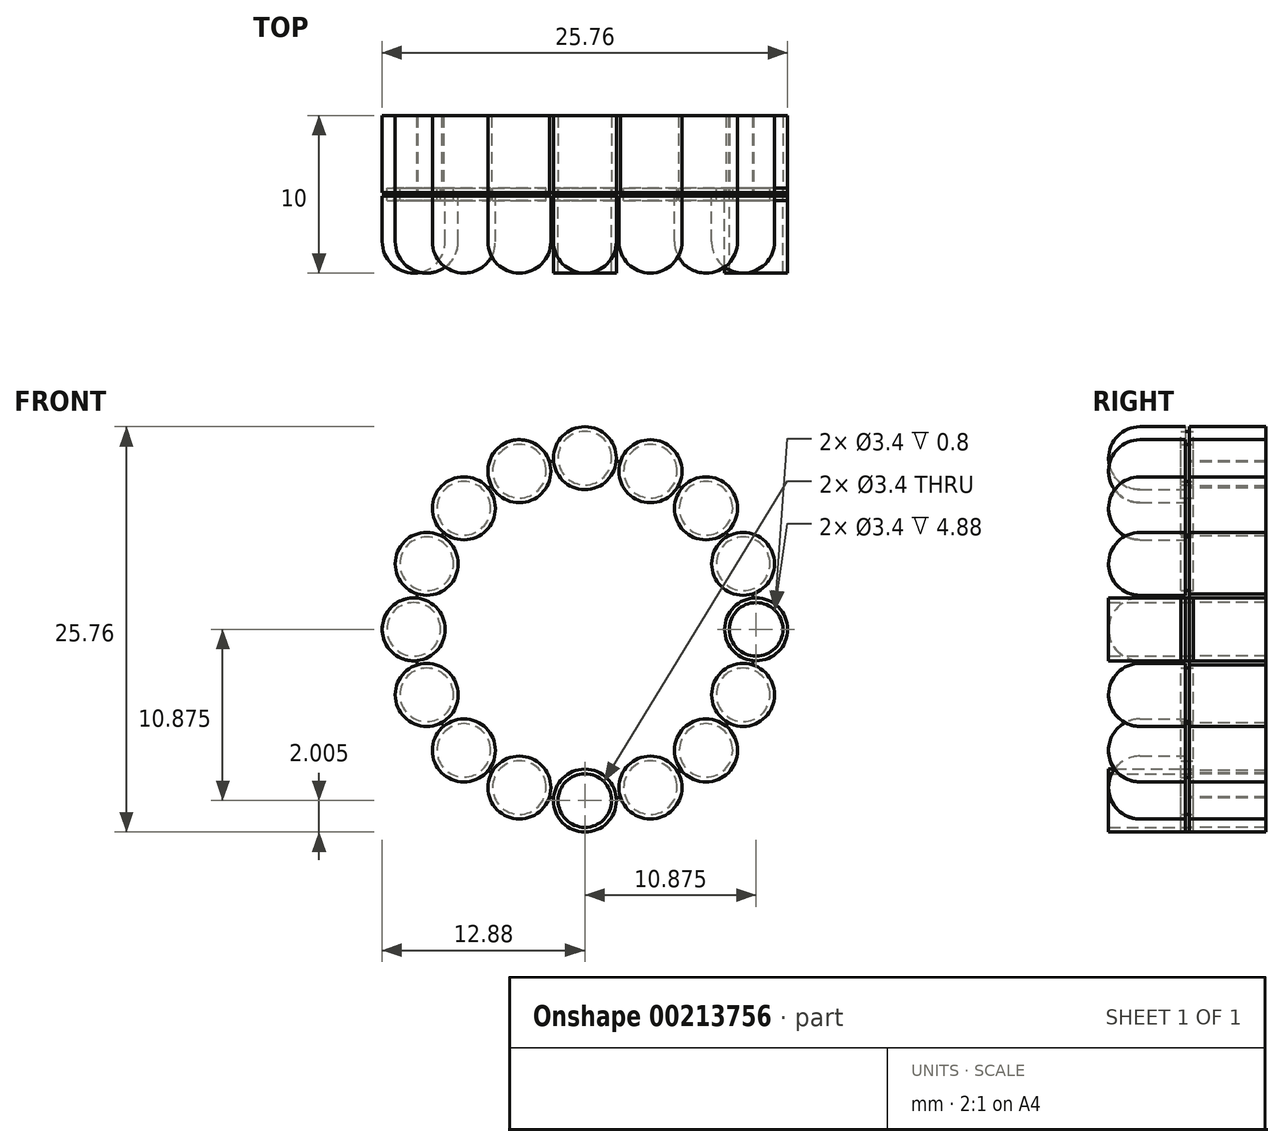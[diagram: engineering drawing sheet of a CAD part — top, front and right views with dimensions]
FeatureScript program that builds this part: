
annotation { "Feature Type Name" : "Feature", "Feature Type Description" : "" }
export const myFeature = defineFeature(function(context is Context, id is Id, definition is map)
    precondition{}
    {
        {
            var Q0;
            Q0=qCreatedBy(makeId("Front.planeOp"),FACE);
            var sketch = newSketch(context, id + "F0", { "sketchPlane" : qUnion([Q0])});
            skCircle(sketch, "E0", {"center": v(0, 0) * mm, "radius": 8.88 * mm, "construction": true});
            skCircle(sketch, "E1.0", {"center": v(0, 0) * mm, "radius": 12.88 * mm, "construction": true});
            skCircle(sketch, "E2.0", {"center": v(0, 0) * mm, "radius": 10.88 * mm});
            skCircle(sketch, "E3", {"center": v(0, 10.88) * mm, "radius": 2 * mm});
            skCircle(sketch, "E4.1.0", {"center": v(-4.16, 10.05) * mm, "radius": 2 * mm});
            skCircle(sketch, "E4.2.0", {"center": v(-7.69, 7.69) * mm, "radius": 2 * mm});
            skCircle(sketch, "E4.3.0", {"center": v(-10.05, 4.16) * mm, "radius": 2 * mm});
            skCircle(sketch, "E4.4.0", {"center": v(-10.88, 0) * mm, "radius": 2 * mm});
            skCircle(sketch, "E4.5.0", {"center": v(-10.05, -4.16) * mm, "radius": 2 * mm});
            skCircle(sketch, "E4.6.0", {"center": v(-7.69, -7.69) * mm, "radius": 2 * mm});
            skCircle(sketch, "E4.7.0", {"center": v(-4.16, -10.05) * mm, "radius": 2 * mm});
            skCircle(sketch, "E4.8.0", {"center": v(0, -10.88) * mm, "radius": 2 * mm});
            skCircle(sketch, "E4.9.0", {"center": v(4.16, -10.05) * mm, "radius": 2 * mm});
            skCircle(sketch, "E4.10.0", {"center": v(7.69, -7.69) * mm, "radius": 2 * mm});
            skCircle(sketch, "E4.11.0", {"center": v(10.05, -4.16) * mm, "radius": 2 * mm});
            skCircle(sketch, "E4.12.0", {"center": v(10.88, 0) * mm, "radius": 2 * mm});
            skCircle(sketch, "E4.13.0", {"center": v(10.05, 4.16) * mm, "radius": 2 * mm});
            skCircle(sketch, "E4.14.0", {"center": v(7.69, 7.69) * mm, "radius": 2 * mm});
            skCircle(sketch, "E4.15.0", {"center": v(4.16, 10.05) * mm, "radius": 2 * mm});
            skCircle(sketch, "E5.0", {"center": v(0, -10.88) * mm, "radius": 1.7 * mm});
            skCircle(sketch, "E6.1.0", {"center": v(4.16, -10.05) * mm, "radius": 1.7 * mm});
            skCircle(sketch, "E6.2.0", {"center": v(7.69, -7.69) * mm, "radius": 1.7 * mm});
            skCircle(sketch, "E6.3.0", {"center": v(10.05, -4.16) * mm, "radius": 1.7 * mm});
            skCircle(sketch, "E6.4.0", {"center": v(10.88, 0) * mm, "radius": 1.7 * mm});
            skCircle(sketch, "E6.5.0", {"center": v(10.05, 4.16) * mm, "radius": 1.7 * mm});
            skCircle(sketch, "E6.6.0", {"center": v(7.69, 7.69) * mm, "radius": 1.7 * mm});
            skCircle(sketch, "E6.7.0", {"center": v(4.16, 10.05) * mm, "radius": 1.7 * mm});
            skCircle(sketch, "E6.8.0", {"center": v(0, 10.88) * mm, "radius": 1.7 * mm});
            skCircle(sketch, "E6.9.0", {"center": v(-4.16, 10.05) * mm, "radius": 1.7 * mm});
            skCircle(sketch, "E6.10.0", {"center": v(-7.69, 7.69) * mm, "radius": 1.7 * mm});
            skCircle(sketch, "E6.11.0", {"center": v(-10.05, 4.16) * mm, "radius": 1.7 * mm});
            skCircle(sketch, "E6.12.0", {"center": v(-10.88, 0) * mm, "radius": 1.7 * mm});
            skCircle(sketch, "E6.13.0", {"center": v(-10.05, -4.16) * mm, "radius": 1.7 * mm});
            skCircle(sketch, "E6.14.0", {"center": v(-7.69, -7.69) * mm, "radius": 1.7 * mm});
            skCircle(sketch, "E6.15.0", {"center": v(-4.16, -10.05) * mm, "radius": 1.7 * mm});
            skSolve(sketch);
        }
        {
            var Q0;
            Q0=makeQuery(id+"F0.imprint","IMPRINT",FACE,{"disambiguationData":[TD([[makeQuery(id+"F0.imprint","IMPRINT",EDGE,{"derivedFrom":sQuery(id+"F0.wireOp",EDGE,"E3")}),1.0]])]});
            var Q1;
            Q1=makeQuery(id+"F0.imprint","IMPRINT",FACE,{"disambiguationData":[TD([[makeQuery(id+"F0.imprint","IMPRINT",EDGE,{"derivedFrom":sQuery(id+"F0.wireOp",EDGE,"E4.15.0")}),1.0]])]});
            var Q2;
            Q2=makeQuery(id+"F0.imprint","IMPRINT",FACE,{"disambiguationData":[TD([[makeQuery(id+"F0.imprint","IMPRINT",EDGE,{"derivedFrom":sQuery(id+"F0.wireOp",EDGE,"E4.14.0")}),1.0]])]});
            var Q3;
            Q3=makeQuery(id+"F0.imprint","IMPRINT",FACE,{"disambiguationData":[TD([[makeQuery(id+"F0.imprint","IMPRINT",EDGE,{"derivedFrom":sQuery(id+"F0.wireOp",EDGE,"E4.13.0")}),1.0]])]});
            var Q4;
            Q4=makeQuery(id+"F0.imprint","IMPRINT",FACE,{"disambiguationData":[TD([[makeQuery(id+"F0.imprint","IMPRINT",EDGE,{"derivedFrom":sQuery(id+"F0.wireOp",EDGE,"E4.12.0")}),1.0]])]});
            var Q5;
            Q5=makeQuery(id+"F0.imprint","IMPRINT",FACE,{"disambiguationData":[TD([[makeQuery(id+"F0.imprint","IMPRINT",EDGE,{"derivedFrom":sQuery(id+"F0.wireOp",EDGE,"E4.11.0")}),1.0]])]});
            var Q6;
            Q6=makeQuery(id+"F0.imprint","IMPRINT",FACE,{"disambiguationData":[TD([[makeQuery(id+"F0.imprint","IMPRINT",EDGE,{"derivedFrom":sQuery(id+"F0.wireOp",EDGE,"E4.10.0")}),1.0]])]});
            var Q7;
            Q7=makeQuery(id+"F0.imprint","IMPRINT",FACE,{"disambiguationData":[TD([[makeQuery(id+"F0.imprint","IMPRINT",EDGE,{"derivedFrom":sQuery(id+"F0.wireOp",EDGE,"E4.9.0")}),1.0]])]});
            var Q8;
            Q8=makeQuery(id+"F0.imprint","IMPRINT",FACE,{"disambiguationData":[TD([[makeQuery(id+"F0.imprint","IMPRINT",EDGE,{"derivedFrom":sQuery(id+"F0.wireOp",EDGE,"E4.8.0")}),1.0]])]});
            var Q9;
            Q9=makeQuery(id+"F0.imprint","IMPRINT",FACE,{"disambiguationData":[TD([[makeQuery(id+"F0.imprint","IMPRINT",EDGE,{"derivedFrom":sQuery(id+"F0.wireOp",EDGE,"E4.7.0")}),1.0]])]});
            var Q10;
            Q10=makeQuery(id+"F0.imprint","IMPRINT",FACE,{"disambiguationData":[TD([[makeQuery(id+"F0.imprint","IMPRINT",EDGE,{"derivedFrom":sQuery(id+"F0.wireOp",EDGE,"E4.6.0")}),1.0]])]});
            var Q11;
            Q11=makeQuery(id+"F0.imprint","IMPRINT",FACE,{"disambiguationData":[TD([[makeQuery(id+"F0.imprint","IMPRINT",EDGE,{"derivedFrom":sQuery(id+"F0.wireOp",EDGE,"E4.5.0")}),1.0]])]});
            var Q12;
            Q12=makeQuery(id+"F0.imprint","IMPRINT",FACE,{"disambiguationData":[TD([[makeQuery(id+"F0.imprint","IMPRINT",EDGE,{"derivedFrom":sQuery(id+"F0.wireOp",EDGE,"E4.4.0")}),1.0]])]});
            var Q13;
            Q13=makeQuery(id+"F0.imprint","IMPRINT",FACE,{"disambiguationData":[TD([[makeQuery(id+"F0.imprint","IMPRINT",EDGE,{"derivedFrom":sQuery(id+"F0.wireOp",EDGE,"E4.3.0")}),1.0]])]});
            var Q14;
            Q14=makeQuery(id+"F0.imprint","IMPRINT",FACE,{"disambiguationData":[TD([[makeQuery(id+"F0.imprint","IMPRINT",EDGE,{"derivedFrom":sQuery(id+"F0.wireOp",EDGE,"E4.2.0")}),1.0]])]});
            var Q15;
            Q15=makeQuery(id+"F0.imprint","IMPRINT",FACE,{"disambiguationData":[TD([[makeQuery(id+"F0.imprint","IMPRINT",EDGE,{"derivedFrom":sQuery(id+"F0.wireOp",EDGE,"E4.1.0")}),1.0]])]});
            var Q16;
            {var subQ0=sQuery(id+"F0.wireOp",EDGE,"E6.3.0");var subQ1=sQuery(id+"F0.wireOp",EDGE,"E2.0");var subQ2=makeQuery(id+"F0.imprint","INTERSECT",VERTEX,{"disambiguationData":[OD(0.0)],"derivedFrom":[subQ1,subQ0]});Q16=makeQuery(id+"F0.imprint","IMPRINT",FACE,{"disambiguationData":[TD([[makeQuery(id+"F0.imprint","IMPRINT",EDGE,{"disambiguationData":[TD([[subQ2,-1.0]])],"derivedFrom":subQ1}),-1.0]])]});}
            var Q17;
            {var subQ0=sQuery(id+"F0.wireOp",EDGE,"E6.3.0");var subQ1=sQuery(id+"F0.wireOp",EDGE,"E2.0");var subQ2=makeQuery(id+"F0.imprint","INTERSECT",VERTEX,{"disambiguationData":[OD(0.0)],"derivedFrom":[subQ1,subQ0]});Q17=makeQuery(id+"F0.imprint","IMPRINT",FACE,{"disambiguationData":[TD([[makeQuery(id+"F0.imprint","IMPRINT",EDGE,{"disambiguationData":[TD([[subQ2,-1.0]])],"derivedFrom":subQ1}),1.0]])]});}
            var Q18;
            {var subQ0=sQuery(id+"F0.wireOp",EDGE,"E6.2.0");var subQ1=sQuery(id+"F0.wireOp",EDGE,"E2.0");var subQ2=makeQuery(id+"F0.imprint","INTERSECT",VERTEX,{"disambiguationData":[OD(0.0)],"derivedFrom":[subQ1,subQ0]});Q18=makeQuery(id+"F0.imprint","IMPRINT",FACE,{"disambiguationData":[TD([[makeQuery(id+"F0.imprint","IMPRINT",EDGE,{"disambiguationData":[TD([[subQ2,-1.0]])],"derivedFrom":subQ1}),-1.0]])]});}
            var Q19;
            {var subQ0=sQuery(id+"F0.wireOp",EDGE,"E6.2.0");var subQ1=sQuery(id+"F0.wireOp",EDGE,"E2.0");var subQ2=makeQuery(id+"F0.imprint","INTERSECT",VERTEX,{"disambiguationData":[OD(0.0)],"derivedFrom":[subQ1,subQ0]});Q19=makeQuery(id+"F0.imprint","IMPRINT",FACE,{"disambiguationData":[TD([[makeQuery(id+"F0.imprint","IMPRINT",EDGE,{"disambiguationData":[TD([[subQ2,-1.0]])],"derivedFrom":subQ1}),1.0]])]});}
            var Q20;
            {var subQ0=sQuery(id+"F0.wireOp",EDGE,"E6.1.0");var subQ1=sQuery(id+"F0.wireOp",EDGE,"E2.0");var subQ2=makeQuery(id+"F0.imprint","INTERSECT",VERTEX,{"disambiguationData":[OD(0.0)],"derivedFrom":[subQ1,subQ0]});Q20=makeQuery(id+"F0.imprint","IMPRINT",FACE,{"disambiguationData":[TD([[makeQuery(id+"F0.imprint","IMPRINT",EDGE,{"disambiguationData":[TD([[subQ2,-1.0]])],"derivedFrom":subQ1}),-1.0]])]});}
            var Q21;
            {var subQ0=sQuery(id+"F0.wireOp",EDGE,"E6.1.0");var subQ1=sQuery(id+"F0.wireOp",EDGE,"E2.0");var subQ2=makeQuery(id+"F0.imprint","INTERSECT",VERTEX,{"disambiguationData":[OD(0.0)],"derivedFrom":[subQ1,subQ0]});Q21=makeQuery(id+"F0.imprint","IMPRINT",FACE,{"disambiguationData":[TD([[makeQuery(id+"F0.imprint","IMPRINT",EDGE,{"disambiguationData":[TD([[subQ2,-1.0]])],"derivedFrom":subQ1}),1.0]])]});}
            var Q22;
            {var subQ0=sQuery(id+"F0.wireOp",EDGE,"E5.0");var subQ1=sQuery(id+"F0.wireOp",EDGE,"E2.0");var subQ2=makeQuery(id+"F0.imprint","INTERSECT",VERTEX,{"disambiguationData":[OD(0.0)],"derivedFrom":[subQ1,subQ0]});Q22=makeQuery(id+"F0.imprint","IMPRINT",FACE,{"disambiguationData":[TD([[makeQuery(id+"F0.imprint","IMPRINT",EDGE,{"disambiguationData":[TD([[subQ2,-1.0]])],"derivedFrom":subQ1}),-1.0]])]});}
            var Q23;
            {var subQ0=sQuery(id+"F0.wireOp",EDGE,"E5.0");var subQ1=sQuery(id+"F0.wireOp",EDGE,"E2.0");var subQ2=makeQuery(id+"F0.imprint","INTERSECT",VERTEX,{"disambiguationData":[OD(0.0)],"derivedFrom":[subQ1,subQ0]});Q23=makeQuery(id+"F0.imprint","IMPRINT",FACE,{"disambiguationData":[TD([[makeQuery(id+"F0.imprint","IMPRINT",EDGE,{"disambiguationData":[TD([[subQ2,-1.0]])],"derivedFrom":subQ1}),1.0]])]});}
            var Q24;
            {var subQ0=sQuery(id+"F0.wireOp",EDGE,"E6.15.0");var subQ1=sQuery(id+"F0.wireOp",EDGE,"E2.0");var subQ2=makeQuery(id+"F0.imprint","INTERSECT",VERTEX,{"disambiguationData":[OD(0.0)],"derivedFrom":[subQ1,subQ0]});Q24=makeQuery(id+"F0.imprint","IMPRINT",FACE,{"disambiguationData":[TD([[makeQuery(id+"F0.imprint","IMPRINT",EDGE,{"disambiguationData":[TD([[subQ2,-1.0]])],"derivedFrom":subQ1}),-1.0]])]});}
            var Q25;
            {var subQ0=sQuery(id+"F0.wireOp",EDGE,"E6.15.0");var subQ1=sQuery(id+"F0.wireOp",EDGE,"E2.0");var subQ2=makeQuery(id+"F0.imprint","INTERSECT",VERTEX,{"disambiguationData":[OD(0.0)],"derivedFrom":[subQ1,subQ0]});Q25=makeQuery(id+"F0.imprint","IMPRINT",FACE,{"disambiguationData":[TD([[makeQuery(id+"F0.imprint","IMPRINT",EDGE,{"disambiguationData":[TD([[subQ2,-1.0]])],"derivedFrom":subQ1}),1.0]])]});}
            var Q26;
            {var subQ0=sQuery(id+"F0.wireOp",EDGE,"E6.14.0");var subQ1=sQuery(id+"F0.wireOp",EDGE,"E2.0");var subQ2=makeQuery(id+"F0.imprint","INTERSECT",VERTEX,{"disambiguationData":[OD(0.0)],"derivedFrom":[subQ1,subQ0]});Q26=makeQuery(id+"F0.imprint","IMPRINT",FACE,{"disambiguationData":[TD([[makeQuery(id+"F0.imprint","IMPRINT",EDGE,{"disambiguationData":[TD([[subQ2,-1.0]])],"derivedFrom":subQ1}),-1.0]])]});}
            var Q27;
            {var subQ0=sQuery(id+"F0.wireOp",EDGE,"E6.14.0");var subQ1=sQuery(id+"F0.wireOp",EDGE,"E2.0");var subQ2=makeQuery(id+"F0.imprint","INTERSECT",VERTEX,{"disambiguationData":[OD(0.0)],"derivedFrom":[subQ1,subQ0]});Q27=makeQuery(id+"F0.imprint","IMPRINT",FACE,{"disambiguationData":[TD([[makeQuery(id+"F0.imprint","IMPRINT",EDGE,{"disambiguationData":[TD([[subQ2,-1.0]])],"derivedFrom":subQ1}),1.0]])]});}
            var Q28;
            {var subQ0=sQuery(id+"F0.wireOp",EDGE,"E6.13.0");var subQ1=sQuery(id+"F0.wireOp",EDGE,"E2.0");var subQ2=makeQuery(id+"F0.imprint","INTERSECT",VERTEX,{"disambiguationData":[OD(0.0)],"derivedFrom":[subQ1,subQ0]});Q28=makeQuery(id+"F0.imprint","IMPRINT",FACE,{"disambiguationData":[TD([[makeQuery(id+"F0.imprint","IMPRINT",EDGE,{"disambiguationData":[TD([[subQ2,-1.0]])],"derivedFrom":subQ1}),-1.0]])]});}
            var Q29;
            {var subQ0=sQuery(id+"F0.wireOp",EDGE,"E6.13.0");var subQ1=sQuery(id+"F0.wireOp",EDGE,"E2.0");var subQ2=makeQuery(id+"F0.imprint","INTERSECT",VERTEX,{"disambiguationData":[OD(0.0)],"derivedFrom":[subQ1,subQ0]});Q29=makeQuery(id+"F0.imprint","IMPRINT",FACE,{"disambiguationData":[TD([[makeQuery(id+"F0.imprint","IMPRINT",EDGE,{"disambiguationData":[TD([[subQ2,-1.0]])],"derivedFrom":subQ1}),1.0]])]});}
            var Q30;
            {var subQ0=sQuery(id+"F0.wireOp",EDGE,"E6.12.0");var subQ1=sQuery(id+"F0.wireOp",EDGE,"E2.0");var subQ2=makeQuery(id+"F0.imprint","INTERSECT",VERTEX,{"disambiguationData":[OD(0.0)],"derivedFrom":[subQ1,subQ0]});Q30=makeQuery(id+"F0.imprint","IMPRINT",FACE,{"disambiguationData":[TD([[makeQuery(id+"F0.imprint","IMPRINT",EDGE,{"disambiguationData":[TD([[subQ2,-1.0]])],"derivedFrom":subQ1}),-1.0]])]});}
            var Q31;
            {var subQ0=sQuery(id+"F0.wireOp",EDGE,"E6.12.0");var subQ1=sQuery(id+"F0.wireOp",EDGE,"E2.0");var subQ2=makeQuery(id+"F0.imprint","INTERSECT",VERTEX,{"disambiguationData":[OD(0.0)],"derivedFrom":[subQ1,subQ0]});Q31=makeQuery(id+"F0.imprint","IMPRINT",FACE,{"disambiguationData":[TD([[makeQuery(id+"F0.imprint","IMPRINT",EDGE,{"disambiguationData":[TD([[subQ2,-1.0]])],"derivedFrom":subQ1}),1.0]])]});}
            var Q32;
            {var subQ0=sQuery(id+"F0.wireOp",EDGE,"E6.11.0");var subQ1=sQuery(id+"F0.wireOp",EDGE,"E2.0");var subQ2=makeQuery(id+"F0.imprint","INTERSECT",VERTEX,{"disambiguationData":[OD(0.0)],"derivedFrom":[subQ1,subQ0]});Q32=makeQuery(id+"F0.imprint","IMPRINT",FACE,{"disambiguationData":[TD([[makeQuery(id+"F0.imprint","IMPRINT",EDGE,{"disambiguationData":[TD([[subQ2,-1.0]])],"derivedFrom":subQ1}),-1.0]])]});}
            var Q33;
            {var subQ0=sQuery(id+"F0.wireOp",EDGE,"E6.11.0");var subQ1=sQuery(id+"F0.wireOp",EDGE,"E2.0");var subQ2=makeQuery(id+"F0.imprint","INTERSECT",VERTEX,{"disambiguationData":[OD(0.0)],"derivedFrom":[subQ1,subQ0]});Q33=makeQuery(id+"F0.imprint","IMPRINT",FACE,{"disambiguationData":[TD([[makeQuery(id+"F0.imprint","IMPRINT",EDGE,{"disambiguationData":[TD([[subQ2,-1.0]])],"derivedFrom":subQ1}),1.0]])]});}
            var Q34;
            {var subQ0=sQuery(id+"F0.wireOp",EDGE,"E6.10.0");var subQ1=sQuery(id+"F0.wireOp",EDGE,"E2.0");var subQ2=makeQuery(id+"F0.imprint","INTERSECT",VERTEX,{"disambiguationData":[OD(0.0)],"derivedFrom":[subQ1,subQ0]});Q34=makeQuery(id+"F0.imprint","IMPRINT",FACE,{"disambiguationData":[TD([[makeQuery(id+"F0.imprint","IMPRINT",EDGE,{"disambiguationData":[TD([[subQ2,-1.0]])],"derivedFrom":subQ1}),-1.0]])]});}
            var Q35;
            {var subQ0=sQuery(id+"F0.wireOp",EDGE,"E6.10.0");var subQ1=sQuery(id+"F0.wireOp",EDGE,"E2.0");var subQ2=makeQuery(id+"F0.imprint","INTERSECT",VERTEX,{"disambiguationData":[OD(0.0)],"derivedFrom":[subQ1,subQ0]});Q35=makeQuery(id+"F0.imprint","IMPRINT",FACE,{"disambiguationData":[TD([[makeQuery(id+"F0.imprint","IMPRINT",EDGE,{"disambiguationData":[TD([[subQ2,-1.0]])],"derivedFrom":subQ1}),1.0]])]});}
            var Q36;
            {var subQ0=sQuery(id+"F0.wireOp",EDGE,"E6.9.0");var subQ1=sQuery(id+"F0.wireOp",EDGE,"E2.0");var subQ2=makeQuery(id+"F0.imprint","INTERSECT",VERTEX,{"disambiguationData":[OD(0.0)],"derivedFrom":[subQ1,subQ0]});Q36=makeQuery(id+"F0.imprint","IMPRINT",FACE,{"disambiguationData":[TD([[makeQuery(id+"F0.imprint","IMPRINT",EDGE,{"disambiguationData":[TD([[subQ2,-1.0]])],"derivedFrom":subQ1}),-1.0]])]});}
            var Q37;
            {var subQ0=sQuery(id+"F0.wireOp",EDGE,"E6.9.0");var subQ1=sQuery(id+"F0.wireOp",EDGE,"E2.0");var subQ2=makeQuery(id+"F0.imprint","INTERSECT",VERTEX,{"disambiguationData":[OD(0.0)],"derivedFrom":[subQ1,subQ0]});Q37=makeQuery(id+"F0.imprint","IMPRINT",FACE,{"disambiguationData":[TD([[makeQuery(id+"F0.imprint","IMPRINT",EDGE,{"disambiguationData":[TD([[subQ2,-1.0]])],"derivedFrom":subQ1}),1.0]])]});}
            var Q38;
            {var subQ0=sQuery(id+"F0.wireOp",EDGE,"E6.8.0");var subQ1=sQuery(id+"F0.wireOp",EDGE,"E2.0");var subQ2=makeQuery(id+"F0.imprint","INTERSECT",VERTEX,{"disambiguationData":[OD(0.0)],"derivedFrom":[subQ1,subQ0]});Q38=makeQuery(id+"F0.imprint","IMPRINT",FACE,{"disambiguationData":[TD([[makeQuery(id+"F0.imprint","IMPRINT",EDGE,{"disambiguationData":[TD([[subQ2,-1.0]])],"derivedFrom":subQ1}),-1.0]])]});}
            var Q39;
            {var subQ0=sQuery(id+"F0.wireOp",EDGE,"E6.8.0");var subQ1=sQuery(id+"F0.wireOp",EDGE,"E2.0");var subQ2=makeQuery(id+"F0.imprint","INTERSECT",VERTEX,{"disambiguationData":[OD(0.0)],"derivedFrom":[subQ1,subQ0]});Q39=makeQuery(id+"F0.imprint","IMPRINT",FACE,{"disambiguationData":[TD([[makeQuery(id+"F0.imprint","IMPRINT",EDGE,{"disambiguationData":[TD([[subQ2,-1.0]])],"derivedFrom":subQ1}),1.0]])]});}
            var Q40;
            {var subQ0=sQuery(id+"F0.wireOp",EDGE,"E6.7.0");var subQ1=sQuery(id+"F0.wireOp",EDGE,"E2.0");var subQ2=makeQuery(id+"F0.imprint","INTERSECT",VERTEX,{"disambiguationData":[OD(0.0)],"derivedFrom":[subQ1,subQ0]});Q40=makeQuery(id+"F0.imprint","IMPRINT",FACE,{"disambiguationData":[TD([[makeQuery(id+"F0.imprint","IMPRINT",EDGE,{"disambiguationData":[TD([[subQ2,-1.0]])],"derivedFrom":subQ1}),-1.0]])]});}
            var Q41;
            {var subQ0=sQuery(id+"F0.wireOp",EDGE,"E6.7.0");var subQ1=sQuery(id+"F0.wireOp",EDGE,"E2.0");var subQ2=makeQuery(id+"F0.imprint","INTERSECT",VERTEX,{"disambiguationData":[OD(0.0)],"derivedFrom":[subQ1,subQ0]});Q41=makeQuery(id+"F0.imprint","IMPRINT",FACE,{"disambiguationData":[TD([[makeQuery(id+"F0.imprint","IMPRINT",EDGE,{"disambiguationData":[TD([[subQ2,-1.0]])],"derivedFrom":subQ1}),1.0]])]});}
            var Q42;
            {var subQ0=sQuery(id+"F0.wireOp",EDGE,"E6.6.0");var subQ1=sQuery(id+"F0.wireOp",EDGE,"E2.0");var subQ2=makeQuery(id+"F0.imprint","INTERSECT",VERTEX,{"disambiguationData":[OD(0.0)],"derivedFrom":[subQ1,subQ0]});Q42=makeQuery(id+"F0.imprint","IMPRINT",FACE,{"disambiguationData":[TD([[makeQuery(id+"F0.imprint","IMPRINT",EDGE,{"disambiguationData":[TD([[subQ2,-1.0]])],"derivedFrom":subQ1}),-1.0]])]});}
            var Q43;
            {var subQ0=sQuery(id+"F0.wireOp",EDGE,"E6.6.0");var subQ1=sQuery(id+"F0.wireOp",EDGE,"E2.0");var subQ2=makeQuery(id+"F0.imprint","INTERSECT",VERTEX,{"disambiguationData":[OD(0.0)],"derivedFrom":[subQ1,subQ0]});Q43=makeQuery(id+"F0.imprint","IMPRINT",FACE,{"disambiguationData":[TD([[makeQuery(id+"F0.imprint","IMPRINT",EDGE,{"disambiguationData":[TD([[subQ2,-1.0]])],"derivedFrom":subQ1}),1.0]])]});}
            var Q44;
            {var subQ0=sQuery(id+"F0.wireOp",EDGE,"E6.5.0");var subQ1=sQuery(id+"F0.wireOp",EDGE,"E2.0");var subQ2=makeQuery(id+"F0.imprint","INTERSECT",VERTEX,{"disambiguationData":[OD(0.0)],"derivedFrom":[subQ1,subQ0]});Q44=makeQuery(id+"F0.imprint","IMPRINT",FACE,{"disambiguationData":[TD([[makeQuery(id+"F0.imprint","IMPRINT",EDGE,{"disambiguationData":[TD([[subQ2,-1.0]])],"derivedFrom":subQ1}),-1.0]])]});}
            var Q45;
            {var subQ0=sQuery(id+"F0.wireOp",EDGE,"E6.5.0");var subQ1=sQuery(id+"F0.wireOp",EDGE,"E2.0");var subQ2=makeQuery(id+"F0.imprint","INTERSECT",VERTEX,{"disambiguationData":[OD(0.0)],"derivedFrom":[subQ1,subQ0]});Q45=makeQuery(id+"F0.imprint","IMPRINT",FACE,{"disambiguationData":[TD([[makeQuery(id+"F0.imprint","IMPRINT",EDGE,{"disambiguationData":[TD([[subQ2,-1.0]])],"derivedFrom":subQ1}),1.0]])]});}
            var Q46;
            {var subQ0=sQuery(id+"F0.wireOp",EDGE,"E6.4.0");var subQ1=sQuery(id+"F0.wireOp",EDGE,"E2.0");var subQ2=makeQuery(id+"F0.imprint","INTERSECT",VERTEX,{"disambiguationData":[OD(0.0)],"derivedFrom":[subQ1,subQ0]});Q46=makeQuery(id+"F0.imprint","IMPRINT",FACE,{"disambiguationData":[TD([[makeQuery(id+"F0.imprint","IMPRINT",EDGE,{"disambiguationData":[TD([[subQ2,1.0]])],"derivedFrom":subQ1}),-1.0]])]});}
            var Q47;
            {var subQ0=sQuery(id+"F0.wireOp",EDGE,"E6.4.0");var subQ1=sQuery(id+"F0.wireOp",EDGE,"E2.0");var subQ2=makeQuery(id+"F0.imprint","INTERSECT",VERTEX,{"disambiguationData":[OD(0.0)],"derivedFrom":[subQ1,subQ0]});Q47=makeQuery(id+"F0.imprint","IMPRINT",FACE,{"disambiguationData":[TD([[makeQuery(id+"F0.imprint","IMPRINT",EDGE,{"disambiguationData":[TD([[subQ2,1.0]])],"derivedFrom":subQ1}),1.0]])]});}
            extrude(context, id + "F1", {"entities" : qUnion([Q0, Q1, Q2, Q3, Q4, Q5, Q6, Q7, Q8, Q9, Q10, Q11, Q12, Q13, Q14, Q15, Q16, Q17, Q18, Q19, Q20, Q21, Q22, Q23, Q24, Q25, Q26, Q27, Q28, Q29, Q30, Q31, Q32, Q33, Q34, Q35, Q36, Q37, Q38, Q39, Q40, Q41, Q42, Q43, Q44, Q45, Q46, Q47]), "depth" : 5 * mm, "hasSecondDirection" : true, "secondDirectionOppositeDirection" : false, "secondDirectionDepth" : .12 * mm});
        }
        {
            var Q0;
            Q0=qCreatedBy(makeId("Right.planeOp"),FACE);
            var sketch = newSketch(context, id + "F2", { "sketchPlane" : qUnion([Q0])});
            skPoint(sketch, "E7", {"position": v(0, -10.88) * mm});
            skLineSegment(sketch, "E8.bottom", {"start": v(-2.5, -11.28) * mm, "end": v(2.5, -11.28) * mm});
            skLineSegment(sketch, "E8.top", {"start": v(-2.5, -10.47) * mm, "end": v(2.5, -10.47) * mm});
            skLineSegment(sketch, "E8.left", {"start": v(-2.5, -11.28) * mm, "end": v(-2.5, -10.47) * mm});
            skLineSegment(sketch, "E8.right", {"start": v(2.5, -11.28) * mm, "end": v(2.5, -10.47) * mm});
            skSolve(sketch);
        }
        {
            var Q0;
            Q0=sQuery(id+"F2.wireOp",EDGE,"E8.right");
            var Q1;
            Q1=sQuery(id+"F2.wireOp",EDGE,"E8.bottom");
            var Q2;
            Q2=sQuery(id+"F2.wireOp",EDGE,"E8.top");
            var Q3;
            Q3=sQuery(id+"F2.wireOp",EDGE,"E8.left");
            var Q4;
            Q4=sQuery(id+"F0.wireOp",EDGE,"E2.0");
            revolve(context, id + "F3", {"bodyType" : ToolBodyType.SURFACE, "surfaceEntities" : qUnion([Q0, Q1, Q2, Q3]), "axis" : qUnion([Q4]), "revolveType" : RevolveType.FULL});
        }
        {
            var Q0;
            {var subQ0=sQuery(id+"F0.wireOp",EDGE,"E6.3.0");var subQ1=sQuery(id+"F0.wireOp",EDGE,"E2.0");var subQ2=makeQuery(id+"F0.imprint","INTERSECT",VERTEX,{"disambiguationData":[OD(0.0)],"derivedFrom":[subQ1,subQ0]});Q0=makeQuery(id+"F0.imprint","IMPRINT",FACE,{"disambiguationData":[TD([[makeQuery(id+"F0.imprint","IMPRINT",EDGE,{"disambiguationData":[TD([[subQ2,-1.0]])],"derivedFrom":subQ1}),-1.0]])]});}
            var Q1;
            {var subQ0=sQuery(id+"F0.wireOp",EDGE,"E4.11.0");var subQ1=sQuery(id+"F0.wireOp",EDGE,"E2.0");var subQ2=makeQuery(id+"F0.imprint","INTERSECT",VERTEX,{"disambiguationData":[OD(0.0)],"derivedFrom":[subQ1,subQ0]});Q1=makeQuery(id+"F0.imprint","IMPRINT",FACE,{"disambiguationData":[TD([[makeQuery(id+"F0.imprint","IMPRINT",EDGE,{"disambiguationData":[TD([[subQ2,-1.0]])],"derivedFrom":subQ1}),-1.0]])]});}
            var Q2;
            {var subQ0=sQuery(id+"F0.wireOp",EDGE,"E6.3.0");var subQ1=sQuery(id+"F0.wireOp",EDGE,"E2.0");var subQ2=makeQuery(id+"F0.imprint","INTERSECT",VERTEX,{"disambiguationData":[OD(0.0)],"derivedFrom":[subQ1,subQ0]});Q2=makeQuery(id+"F0.imprint","IMPRINT",FACE,{"disambiguationData":[TD([[makeQuery(id+"F0.imprint","IMPRINT",EDGE,{"disambiguationData":[TD([[subQ2,-1.0]])],"derivedFrom":subQ1}),1.0]])]});}
            var Q3;
            {var subQ0=sQuery(id+"F0.wireOp",EDGE,"E4.11.0");var subQ1=sQuery(id+"F0.wireOp",EDGE,"E2.0");var subQ2=makeQuery(id+"F0.imprint","INTERSECT",VERTEX,{"disambiguationData":[OD(0.0)],"derivedFrom":[subQ1,subQ0]});Q3=makeQuery(id+"F0.imprint","IMPRINT",FACE,{"disambiguationData":[TD([[makeQuery(id+"F0.imprint","IMPRINT",EDGE,{"disambiguationData":[TD([[subQ2,-1.0]])],"derivedFrom":subQ1}),1.0]])]});}
            var Q4;
            {var subQ0=sQuery(id+"F0.wireOp",EDGE,"E4.10.0");var subQ1=sQuery(id+"F0.wireOp",EDGE,"E2.0");var subQ2=makeQuery(id+"F0.imprint","INTERSECT",VERTEX,{"disambiguationData":[OD(0.0)],"derivedFrom":[subQ1,subQ0]});Q4=makeQuery(id+"F0.imprint","IMPRINT",FACE,{"disambiguationData":[TD([[makeQuery(id+"F0.imprint","IMPRINT",EDGE,{"disambiguationData":[TD([[subQ2,-1.0]])],"derivedFrom":subQ1}),1.0]])]});}
            var Q5;
            {var subQ0=sQuery(id+"F0.wireOp",EDGE,"E6.2.0");var subQ1=sQuery(id+"F0.wireOp",EDGE,"E2.0");var subQ2=makeQuery(id+"F0.imprint","INTERSECT",VERTEX,{"disambiguationData":[OD(0.0)],"derivedFrom":[subQ1,subQ0]});Q5=makeQuery(id+"F0.imprint","IMPRINT",FACE,{"disambiguationData":[TD([[makeQuery(id+"F0.imprint","IMPRINT",EDGE,{"disambiguationData":[TD([[subQ2,-1.0]])],"derivedFrom":subQ1}),1.0]])]});}
            var Q6;
            {var subQ0=sQuery(id+"F0.wireOp",EDGE,"E6.2.0");var subQ1=sQuery(id+"F0.wireOp",EDGE,"E2.0");var subQ2=makeQuery(id+"F0.imprint","INTERSECT",VERTEX,{"disambiguationData":[OD(0.0)],"derivedFrom":[subQ1,subQ0]});Q6=makeQuery(id+"F0.imprint","IMPRINT",FACE,{"disambiguationData":[TD([[makeQuery(id+"F0.imprint","IMPRINT",EDGE,{"disambiguationData":[TD([[subQ2,-1.0]])],"derivedFrom":subQ1}),-1.0]])]});}
            var Q7;
            {var subQ0=sQuery(id+"F0.wireOp",EDGE,"E4.10.0");var subQ1=sQuery(id+"F0.wireOp",EDGE,"E2.0");var subQ2=makeQuery(id+"F0.imprint","INTERSECT",VERTEX,{"disambiguationData":[OD(0.0)],"derivedFrom":[subQ1,subQ0]});Q7=makeQuery(id+"F0.imprint","IMPRINT",FACE,{"disambiguationData":[TD([[makeQuery(id+"F0.imprint","IMPRINT",EDGE,{"disambiguationData":[TD([[subQ2,-1.0]])],"derivedFrom":subQ1}),-1.0]])]});}
            var Q8;
            {var subQ0=sQuery(id+"F0.wireOp",EDGE,"E4.9.0");var subQ1=sQuery(id+"F0.wireOp",EDGE,"E2.0");var subQ2=makeQuery(id+"F0.imprint","INTERSECT",VERTEX,{"disambiguationData":[OD(0.0)],"derivedFrom":[subQ1,subQ0]});Q8=makeQuery(id+"F0.imprint","IMPRINT",FACE,{"disambiguationData":[TD([[makeQuery(id+"F0.imprint","IMPRINT",EDGE,{"disambiguationData":[TD([[subQ2,-1.0]])],"derivedFrom":subQ1}),-1.0]])]});}
            var Q9;
            {var subQ0=sQuery(id+"F0.wireOp",EDGE,"E6.1.0");var subQ1=sQuery(id+"F0.wireOp",EDGE,"E2.0");var subQ2=makeQuery(id+"F0.imprint","INTERSECT",VERTEX,{"disambiguationData":[OD(0.0)],"derivedFrom":[subQ1,subQ0]});Q9=makeQuery(id+"F0.imprint","IMPRINT",FACE,{"disambiguationData":[TD([[makeQuery(id+"F0.imprint","IMPRINT",EDGE,{"disambiguationData":[TD([[subQ2,-1.0]])],"derivedFrom":subQ1}),-1.0]])]});}
            var Q10;
            {var subQ0=sQuery(id+"F0.wireOp",EDGE,"E6.1.0");var subQ1=sQuery(id+"F0.wireOp",EDGE,"E2.0");var subQ2=makeQuery(id+"F0.imprint","INTERSECT",VERTEX,{"disambiguationData":[OD(0.0)],"derivedFrom":[subQ1,subQ0]});Q10=makeQuery(id+"F0.imprint","IMPRINT",FACE,{"disambiguationData":[TD([[makeQuery(id+"F0.imprint","IMPRINT",EDGE,{"disambiguationData":[TD([[subQ2,-1.0]])],"derivedFrom":subQ1}),1.0]])]});}
            var Q11;
            {var subQ0=sQuery(id+"F0.wireOp",EDGE,"E4.9.0");var subQ1=sQuery(id+"F0.wireOp",EDGE,"E2.0");var subQ2=makeQuery(id+"F0.imprint","INTERSECT",VERTEX,{"disambiguationData":[OD(0.0)],"derivedFrom":[subQ1,subQ0]});Q11=makeQuery(id+"F0.imprint","IMPRINT",FACE,{"disambiguationData":[TD([[makeQuery(id+"F0.imprint","IMPRINT",EDGE,{"disambiguationData":[TD([[subQ2,-1.0]])],"derivedFrom":subQ1}),1.0]])]});}
            var Q12;
            {var subQ0=sQuery(id+"F0.wireOp",EDGE,"E5.0");var subQ1=sQuery(id+"F0.wireOp",EDGE,"E2.0");var subQ2=makeQuery(id+"F0.imprint","INTERSECT",VERTEX,{"disambiguationData":[OD(0.0)],"derivedFrom":[subQ1,subQ0]});Q12=makeQuery(id+"F0.imprint","IMPRINT",FACE,{"disambiguationData":[TD([[makeQuery(id+"F0.imprint","IMPRINT",EDGE,{"disambiguationData":[TD([[subQ2,-1.0]])],"derivedFrom":subQ1}),1.0]])]});}
            var Q13;
            {var subQ0=sQuery(id+"F0.wireOp",EDGE,"E5.0");var subQ1=sQuery(id+"F0.wireOp",EDGE,"E2.0");var subQ2=makeQuery(id+"F0.imprint","INTERSECT",VERTEX,{"disambiguationData":[OD(0.0)],"derivedFrom":[subQ1,subQ0]});Q13=makeQuery(id+"F0.imprint","IMPRINT",FACE,{"disambiguationData":[TD([[makeQuery(id+"F0.imprint","IMPRINT",EDGE,{"disambiguationData":[TD([[subQ2,-1.0]])],"derivedFrom":subQ1}),-1.0]])]});}
            var Q14;
            {var subQ0=sQuery(id+"F0.wireOp",EDGE,"E4.8.0");var subQ1=sQuery(id+"F0.wireOp",EDGE,"E2.0");var subQ2=makeQuery(id+"F0.imprint","INTERSECT",VERTEX,{"disambiguationData":[OD(0.0)],"derivedFrom":[subQ1,subQ0]});Q14=makeQuery(id+"F0.imprint","IMPRINT",FACE,{"disambiguationData":[TD([[makeQuery(id+"F0.imprint","IMPRINT",EDGE,{"disambiguationData":[TD([[subQ2,-1.0]])],"derivedFrom":subQ1}),-1.0]])]});}
            var Q15;
            {var subQ0=sQuery(id+"F0.wireOp",EDGE,"E4.8.0");var subQ1=sQuery(id+"F0.wireOp",EDGE,"E2.0");var subQ2=makeQuery(id+"F0.imprint","INTERSECT",VERTEX,{"disambiguationData":[OD(0.0)],"derivedFrom":[subQ1,subQ0]});Q15=makeQuery(id+"F0.imprint","IMPRINT",FACE,{"disambiguationData":[TD([[makeQuery(id+"F0.imprint","IMPRINT",EDGE,{"disambiguationData":[TD([[subQ2,-1.0]])],"derivedFrom":subQ1}),1.0]])]});}
            var Q16;
            {var subQ0=sQuery(id+"F0.wireOp",EDGE,"E4.7.0");var subQ1=sQuery(id+"F0.wireOp",EDGE,"E2.0");var subQ2=makeQuery(id+"F0.imprint","INTERSECT",VERTEX,{"disambiguationData":[OD(0.0)],"derivedFrom":[subQ1,subQ0]});Q16=makeQuery(id+"F0.imprint","IMPRINT",FACE,{"disambiguationData":[TD([[makeQuery(id+"F0.imprint","IMPRINT",EDGE,{"disambiguationData":[TD([[subQ2,-1.0]])],"derivedFrom":subQ1}),1.0]])]});}
            var Q17;
            {var subQ0=sQuery(id+"F0.wireOp",EDGE,"E6.15.0");var subQ1=sQuery(id+"F0.wireOp",EDGE,"E2.0");var subQ2=makeQuery(id+"F0.imprint","INTERSECT",VERTEX,{"disambiguationData":[OD(0.0)],"derivedFrom":[subQ1,subQ0]});Q17=makeQuery(id+"F0.imprint","IMPRINT",FACE,{"disambiguationData":[TD([[makeQuery(id+"F0.imprint","IMPRINT",EDGE,{"disambiguationData":[TD([[subQ2,-1.0]])],"derivedFrom":subQ1}),1.0]])]});}
            var Q18;
            {var subQ0=sQuery(id+"F0.wireOp",EDGE,"E6.15.0");var subQ1=sQuery(id+"F0.wireOp",EDGE,"E2.0");var subQ2=makeQuery(id+"F0.imprint","INTERSECT",VERTEX,{"disambiguationData":[OD(0.0)],"derivedFrom":[subQ1,subQ0]});Q18=makeQuery(id+"F0.imprint","IMPRINT",FACE,{"disambiguationData":[TD([[makeQuery(id+"F0.imprint","IMPRINT",EDGE,{"disambiguationData":[TD([[subQ2,-1.0]])],"derivedFrom":subQ1}),-1.0]])]});}
            var Q19;
            {var subQ0=sQuery(id+"F0.wireOp",EDGE,"E4.7.0");var subQ1=sQuery(id+"F0.wireOp",EDGE,"E2.0");var subQ2=makeQuery(id+"F0.imprint","INTERSECT",VERTEX,{"disambiguationData":[OD(0.0)],"derivedFrom":[subQ1,subQ0]});Q19=makeQuery(id+"F0.imprint","IMPRINT",FACE,{"disambiguationData":[TD([[makeQuery(id+"F0.imprint","IMPRINT",EDGE,{"disambiguationData":[TD([[subQ2,-1.0]])],"derivedFrom":subQ1}),-1.0]])]});}
            var Q20;
            {var subQ0=sQuery(id+"F0.wireOp",EDGE,"E4.6.0");var subQ1=sQuery(id+"F0.wireOp",EDGE,"E2.0");var subQ2=makeQuery(id+"F0.imprint","INTERSECT",VERTEX,{"disambiguationData":[OD(0.0)],"derivedFrom":[subQ1,subQ0]});Q20=makeQuery(id+"F0.imprint","IMPRINT",FACE,{"disambiguationData":[TD([[makeQuery(id+"F0.imprint","IMPRINT",EDGE,{"disambiguationData":[TD([[subQ2,-1.0]])],"derivedFrom":subQ1}),-1.0]])]});}
            var Q21;
            {var subQ0=sQuery(id+"F0.wireOp",EDGE,"E6.14.0");var subQ1=sQuery(id+"F0.wireOp",EDGE,"E2.0");var subQ2=makeQuery(id+"F0.imprint","INTERSECT",VERTEX,{"disambiguationData":[OD(0.0)],"derivedFrom":[subQ1,subQ0]});Q21=makeQuery(id+"F0.imprint","IMPRINT",FACE,{"disambiguationData":[TD([[makeQuery(id+"F0.imprint","IMPRINT",EDGE,{"disambiguationData":[TD([[subQ2,-1.0]])],"derivedFrom":subQ1}),-1.0]])]});}
            var Q22;
            {var subQ0=sQuery(id+"F0.wireOp",EDGE,"E6.14.0");var subQ1=sQuery(id+"F0.wireOp",EDGE,"E2.0");var subQ2=makeQuery(id+"F0.imprint","INTERSECT",VERTEX,{"disambiguationData":[OD(0.0)],"derivedFrom":[subQ1,subQ0]});Q22=makeQuery(id+"F0.imprint","IMPRINT",FACE,{"disambiguationData":[TD([[makeQuery(id+"F0.imprint","IMPRINT",EDGE,{"disambiguationData":[TD([[subQ2,-1.0]])],"derivedFrom":subQ1}),1.0]])]});}
            var Q23;
            {var subQ0=sQuery(id+"F0.wireOp",EDGE,"E4.6.0");var subQ1=sQuery(id+"F0.wireOp",EDGE,"E2.0");var subQ2=makeQuery(id+"F0.imprint","INTERSECT",VERTEX,{"disambiguationData":[OD(0.0)],"derivedFrom":[subQ1,subQ0]});Q23=makeQuery(id+"F0.imprint","IMPRINT",FACE,{"disambiguationData":[TD([[makeQuery(id+"F0.imprint","IMPRINT",EDGE,{"disambiguationData":[TD([[subQ2,-1.0]])],"derivedFrom":subQ1}),1.0]])]});}
            var Q24;
            {var subQ0=sQuery(id+"F0.wireOp",EDGE,"E6.13.0");var subQ1=sQuery(id+"F0.wireOp",EDGE,"E2.0");var subQ2=makeQuery(id+"F0.imprint","INTERSECT",VERTEX,{"disambiguationData":[OD(0.0)],"derivedFrom":[subQ1,subQ0]});Q24=makeQuery(id+"F0.imprint","IMPRINT",FACE,{"disambiguationData":[TD([[makeQuery(id+"F0.imprint","IMPRINT",EDGE,{"disambiguationData":[TD([[subQ2,-1.0]])],"derivedFrom":subQ1}),1.0]])]});}
            var Q25;
            {var subQ0=sQuery(id+"F0.wireOp",EDGE,"E4.5.0");var subQ1=sQuery(id+"F0.wireOp",EDGE,"E2.0");var subQ2=makeQuery(id+"F0.imprint","INTERSECT",VERTEX,{"disambiguationData":[OD(0.0)],"derivedFrom":[subQ1,subQ0]});Q25=makeQuery(id+"F0.imprint","IMPRINT",FACE,{"disambiguationData":[TD([[makeQuery(id+"F0.imprint","IMPRINT",EDGE,{"disambiguationData":[TD([[subQ2,-1.0]])],"derivedFrom":subQ1}),1.0]])]});}
            var Q26;
            {var subQ0=sQuery(id+"F0.wireOp",EDGE,"E6.13.0");var subQ1=sQuery(id+"F0.wireOp",EDGE,"E2.0");var subQ2=makeQuery(id+"F0.imprint","INTERSECT",VERTEX,{"disambiguationData":[OD(0.0)],"derivedFrom":[subQ1,subQ0]});Q26=makeQuery(id+"F0.imprint","IMPRINT",FACE,{"disambiguationData":[TD([[makeQuery(id+"F0.imprint","IMPRINT",EDGE,{"disambiguationData":[TD([[subQ2,-1.0]])],"derivedFrom":subQ1}),-1.0]])]});}
            var Q27;
            {var subQ0=sQuery(id+"F0.wireOp",EDGE,"E4.5.0");var subQ1=sQuery(id+"F0.wireOp",EDGE,"E2.0");var subQ2=makeQuery(id+"F0.imprint","INTERSECT",VERTEX,{"disambiguationData":[OD(0.0)],"derivedFrom":[subQ1,subQ0]});Q27=makeQuery(id+"F0.imprint","IMPRINT",FACE,{"disambiguationData":[TD([[makeQuery(id+"F0.imprint","IMPRINT",EDGE,{"disambiguationData":[TD([[subQ2,-1.0]])],"derivedFrom":subQ1}),-1.0]])]});}
            var Q28;
            {var subQ0=sQuery(id+"F0.wireOp",EDGE,"E4.4.0");var subQ1=sQuery(id+"F0.wireOp",EDGE,"E2.0");var subQ2=makeQuery(id+"F0.imprint","INTERSECT",VERTEX,{"disambiguationData":[OD(0.0)],"derivedFrom":[subQ1,subQ0]});Q28=makeQuery(id+"F0.imprint","IMPRINT",FACE,{"disambiguationData":[TD([[makeQuery(id+"F0.imprint","IMPRINT",EDGE,{"disambiguationData":[TD([[subQ2,-1.0]])],"derivedFrom":subQ1}),-1.0]])]});}
            var Q29;
            {var subQ0=sQuery(id+"F0.wireOp",EDGE,"E6.12.0");var subQ1=sQuery(id+"F0.wireOp",EDGE,"E2.0");var subQ2=makeQuery(id+"F0.imprint","INTERSECT",VERTEX,{"disambiguationData":[OD(0.0)],"derivedFrom":[subQ1,subQ0]});Q29=makeQuery(id+"F0.imprint","IMPRINT",FACE,{"disambiguationData":[TD([[makeQuery(id+"F0.imprint","IMPRINT",EDGE,{"disambiguationData":[TD([[subQ2,-1.0]])],"derivedFrom":subQ1}),-1.0]])]});}
            var Q30;
            {var subQ0=sQuery(id+"F0.wireOp",EDGE,"E6.12.0");var subQ1=sQuery(id+"F0.wireOp",EDGE,"E2.0");var subQ2=makeQuery(id+"F0.imprint","INTERSECT",VERTEX,{"disambiguationData":[OD(0.0)],"derivedFrom":[subQ1,subQ0]});Q30=makeQuery(id+"F0.imprint","IMPRINT",FACE,{"disambiguationData":[TD([[makeQuery(id+"F0.imprint","IMPRINT",EDGE,{"disambiguationData":[TD([[subQ2,-1.0]])],"derivedFrom":subQ1}),1.0]])]});}
            var Q31;
            {var subQ0=sQuery(id+"F0.wireOp",EDGE,"E4.4.0");var subQ1=sQuery(id+"F0.wireOp",EDGE,"E2.0");var subQ2=makeQuery(id+"F0.imprint","INTERSECT",VERTEX,{"disambiguationData":[OD(0.0)],"derivedFrom":[subQ1,subQ0]});Q31=makeQuery(id+"F0.imprint","IMPRINT",FACE,{"disambiguationData":[TD([[makeQuery(id+"F0.imprint","IMPRINT",EDGE,{"disambiguationData":[TD([[subQ2,-1.0]])],"derivedFrom":subQ1}),1.0]])]});}
            var Q32;
            {var subQ0=sQuery(id+"F0.wireOp",EDGE,"E4.3.0");var subQ1=sQuery(id+"F0.wireOp",EDGE,"E2.0");var subQ2=makeQuery(id+"F0.imprint","INTERSECT",VERTEX,{"disambiguationData":[OD(0.0)],"derivedFrom":[subQ1,subQ0]});Q32=makeQuery(id+"F0.imprint","IMPRINT",FACE,{"disambiguationData":[TD([[makeQuery(id+"F0.imprint","IMPRINT",EDGE,{"disambiguationData":[TD([[subQ2,-1.0]])],"derivedFrom":subQ1}),1.0]])]});}
            var Q33;
            {var subQ0=sQuery(id+"F0.wireOp",EDGE,"E6.11.0");var subQ1=sQuery(id+"F0.wireOp",EDGE,"E2.0");var subQ2=makeQuery(id+"F0.imprint","INTERSECT",VERTEX,{"disambiguationData":[OD(0.0)],"derivedFrom":[subQ1,subQ0]});Q33=makeQuery(id+"F0.imprint","IMPRINT",FACE,{"disambiguationData":[TD([[makeQuery(id+"F0.imprint","IMPRINT",EDGE,{"disambiguationData":[TD([[subQ2,-1.0]])],"derivedFrom":subQ1}),1.0]])]});}
            var Q34;
            {var subQ0=sQuery(id+"F0.wireOp",EDGE,"E6.11.0");var subQ1=sQuery(id+"F0.wireOp",EDGE,"E2.0");var subQ2=makeQuery(id+"F0.imprint","INTERSECT",VERTEX,{"disambiguationData":[OD(0.0)],"derivedFrom":[subQ1,subQ0]});Q34=makeQuery(id+"F0.imprint","IMPRINT",FACE,{"disambiguationData":[TD([[makeQuery(id+"F0.imprint","IMPRINT",EDGE,{"disambiguationData":[TD([[subQ2,-1.0]])],"derivedFrom":subQ1}),-1.0]])]});}
            var Q35;
            {var subQ0=sQuery(id+"F0.wireOp",EDGE,"E4.3.0");var subQ1=sQuery(id+"F0.wireOp",EDGE,"E2.0");var subQ2=makeQuery(id+"F0.imprint","INTERSECT",VERTEX,{"disambiguationData":[OD(0.0)],"derivedFrom":[subQ1,subQ0]});Q35=makeQuery(id+"F0.imprint","IMPRINT",FACE,{"disambiguationData":[TD([[makeQuery(id+"F0.imprint","IMPRINT",EDGE,{"disambiguationData":[TD([[subQ2,-1.0]])],"derivedFrom":subQ1}),-1.0]])]});}
            var Q36;
            {var subQ0=sQuery(id+"F0.wireOp",EDGE,"E6.10.0");var subQ1=sQuery(id+"F0.wireOp",EDGE,"E2.0");var subQ2=makeQuery(id+"F0.imprint","INTERSECT",VERTEX,{"disambiguationData":[OD(0.0)],"derivedFrom":[subQ1,subQ0]});Q36=makeQuery(id+"F0.imprint","IMPRINT",FACE,{"disambiguationData":[TD([[makeQuery(id+"F0.imprint","IMPRINT",EDGE,{"disambiguationData":[TD([[subQ2,-1.0]])],"derivedFrom":subQ1}),-1.0]])]});}
            var Q37;
            {var subQ0=sQuery(id+"F0.wireOp",EDGE,"E6.10.0");var subQ1=sQuery(id+"F0.wireOp",EDGE,"E2.0");var subQ2=makeQuery(id+"F0.imprint","INTERSECT",VERTEX,{"disambiguationData":[OD(0.0)],"derivedFrom":[subQ1,subQ0]});Q37=makeQuery(id+"F0.imprint","IMPRINT",FACE,{"disambiguationData":[TD([[makeQuery(id+"F0.imprint","IMPRINT",EDGE,{"disambiguationData":[TD([[subQ2,-1.0]])],"derivedFrom":subQ1}),1.0]])]});}
            var Q38;
            {var subQ0=sQuery(id+"F0.wireOp",EDGE,"E4.2.0");var subQ1=sQuery(id+"F0.wireOp",EDGE,"E2.0");var subQ2=makeQuery(id+"F0.imprint","INTERSECT",VERTEX,{"disambiguationData":[OD(0.0)],"derivedFrom":[subQ1,subQ0]});Q38=makeQuery(id+"F0.imprint","IMPRINT",FACE,{"disambiguationData":[TD([[makeQuery(id+"F0.imprint","IMPRINT",EDGE,{"disambiguationData":[TD([[subQ2,-1.0]])],"derivedFrom":subQ1}),1.0]])]});}
            var Q39;
            {var subQ0=sQuery(id+"F0.wireOp",EDGE,"E4.2.0");var subQ1=sQuery(id+"F0.wireOp",EDGE,"E2.0");var subQ2=makeQuery(id+"F0.imprint","INTERSECT",VERTEX,{"disambiguationData":[OD(0.0)],"derivedFrom":[subQ1,subQ0]});Q39=makeQuery(id+"F0.imprint","IMPRINT",FACE,{"disambiguationData":[TD([[makeQuery(id+"F0.imprint","IMPRINT",EDGE,{"disambiguationData":[TD([[subQ2,-1.0]])],"derivedFrom":subQ1}),-1.0]])]});}
            var Q40;
            {var subQ0=sQuery(id+"F0.wireOp",EDGE,"E6.9.0");var subQ1=sQuery(id+"F0.wireOp",EDGE,"E2.0");var subQ2=makeQuery(id+"F0.imprint","INTERSECT",VERTEX,{"disambiguationData":[OD(0.0)],"derivedFrom":[subQ1,subQ0]});Q40=makeQuery(id+"F0.imprint","IMPRINT",FACE,{"disambiguationData":[TD([[makeQuery(id+"F0.imprint","IMPRINT",EDGE,{"disambiguationData":[TD([[subQ2,-1.0]])],"derivedFrom":subQ1}),1.0]])]});}
            var Q41;
            {var subQ0=sQuery(id+"F0.wireOp",EDGE,"E6.9.0");var subQ1=sQuery(id+"F0.wireOp",EDGE,"E2.0");var subQ2=makeQuery(id+"F0.imprint","INTERSECT",VERTEX,{"disambiguationData":[OD(0.0)],"derivedFrom":[subQ1,subQ0]});Q41=makeQuery(id+"F0.imprint","IMPRINT",FACE,{"disambiguationData":[TD([[makeQuery(id+"F0.imprint","IMPRINT",EDGE,{"disambiguationData":[TD([[subQ2,-1.0]])],"derivedFrom":subQ1}),-1.0]])]});}
            var Q42;
            {var subQ0=sQuery(id+"F0.wireOp",EDGE,"E4.1.0");var subQ1=sQuery(id+"F0.wireOp",EDGE,"E2.0");var subQ2=makeQuery(id+"F0.imprint","INTERSECT",VERTEX,{"disambiguationData":[OD(0.0)],"derivedFrom":[subQ1,subQ0]});Q42=makeQuery(id+"F0.imprint","IMPRINT",FACE,{"disambiguationData":[TD([[makeQuery(id+"F0.imprint","IMPRINT",EDGE,{"disambiguationData":[TD([[subQ2,-1.0]])],"derivedFrom":subQ1}),1.0]])]});}
            var Q43;
            {var subQ0=sQuery(id+"F0.wireOp",EDGE,"E4.1.0");var subQ1=sQuery(id+"F0.wireOp",EDGE,"E2.0");var subQ2=makeQuery(id+"F0.imprint","INTERSECT",VERTEX,{"disambiguationData":[OD(0.0)],"derivedFrom":[subQ1,subQ0]});Q43=makeQuery(id+"F0.imprint","IMPRINT",FACE,{"disambiguationData":[TD([[makeQuery(id+"F0.imprint","IMPRINT",EDGE,{"disambiguationData":[TD([[subQ2,-1.0]])],"derivedFrom":subQ1}),-1.0]])]});}
            var Q44;
            {var subQ0=sQuery(id+"F0.wireOp",EDGE,"E3");var subQ1=sQuery(id+"F0.wireOp",EDGE,"E2.0");var subQ2=makeQuery(id+"F0.imprint","INTERSECT",VERTEX,{"disambiguationData":[OD(0.0)],"derivedFrom":[subQ1,subQ0]});Q44=makeQuery(id+"F0.imprint","IMPRINT",FACE,{"disambiguationData":[TD([[makeQuery(id+"F0.imprint","IMPRINT",EDGE,{"disambiguationData":[TD([[subQ2,-1.0]])],"derivedFrom":subQ1}),-1.0]])]});}
            var Q45;
            {var subQ0=sQuery(id+"F0.wireOp",EDGE,"E6.8.0");var subQ1=sQuery(id+"F0.wireOp",EDGE,"E2.0");var subQ2=makeQuery(id+"F0.imprint","INTERSECT",VERTEX,{"disambiguationData":[OD(0.0)],"derivedFrom":[subQ1,subQ0]});Q45=makeQuery(id+"F0.imprint","IMPRINT",FACE,{"disambiguationData":[TD([[makeQuery(id+"F0.imprint","IMPRINT",EDGE,{"disambiguationData":[TD([[subQ2,-1.0]])],"derivedFrom":subQ1}),-1.0]])]});}
            var Q46;
            {var subQ0=sQuery(id+"F0.wireOp",EDGE,"E6.8.0");var subQ1=sQuery(id+"F0.wireOp",EDGE,"E2.0");var subQ2=makeQuery(id+"F0.imprint","INTERSECT",VERTEX,{"disambiguationData":[OD(0.0)],"derivedFrom":[subQ1,subQ0]});Q46=makeQuery(id+"F0.imprint","IMPRINT",FACE,{"disambiguationData":[TD([[makeQuery(id+"F0.imprint","IMPRINT",EDGE,{"disambiguationData":[TD([[subQ2,-1.0]])],"derivedFrom":subQ1}),1.0]])]});}
            var Q47;
            {var subQ0=sQuery(id+"F0.wireOp",EDGE,"E3");var subQ1=sQuery(id+"F0.wireOp",EDGE,"E2.0");var subQ2=makeQuery(id+"F0.imprint","INTERSECT",VERTEX,{"disambiguationData":[OD(0.0)],"derivedFrom":[subQ1,subQ0]});Q47=makeQuery(id+"F0.imprint","IMPRINT",FACE,{"disambiguationData":[TD([[makeQuery(id+"F0.imprint","IMPRINT",EDGE,{"disambiguationData":[TD([[subQ2,-1.0]])],"derivedFrom":subQ1}),1.0]])]});}
            var Q48;
            {var subQ0=sQuery(id+"F0.wireOp",EDGE,"E4.15.0");var subQ1=sQuery(id+"F0.wireOp",EDGE,"E2.0");var subQ2=makeQuery(id+"F0.imprint","INTERSECT",VERTEX,{"disambiguationData":[OD(0.0)],"derivedFrom":[subQ1,subQ0]});Q48=makeQuery(id+"F0.imprint","IMPRINT",FACE,{"disambiguationData":[TD([[makeQuery(id+"F0.imprint","IMPRINT",EDGE,{"disambiguationData":[TD([[subQ2,-1.0]])],"derivedFrom":subQ1}),1.0]])]});}
            var Q49;
            {var subQ0=sQuery(id+"F0.wireOp",EDGE,"E6.7.0");var subQ1=sQuery(id+"F0.wireOp",EDGE,"E2.0");var subQ2=makeQuery(id+"F0.imprint","INTERSECT",VERTEX,{"disambiguationData":[OD(0.0)],"derivedFrom":[subQ1,subQ0]});Q49=makeQuery(id+"F0.imprint","IMPRINT",FACE,{"disambiguationData":[TD([[makeQuery(id+"F0.imprint","IMPRINT",EDGE,{"disambiguationData":[TD([[subQ2,-1.0]])],"derivedFrom":subQ1}),1.0]])]});}
            var Q50;
            {var subQ0=sQuery(id+"F0.wireOp",EDGE,"E6.7.0");var subQ1=sQuery(id+"F0.wireOp",EDGE,"E2.0");var subQ2=makeQuery(id+"F0.imprint","INTERSECT",VERTEX,{"disambiguationData":[OD(0.0)],"derivedFrom":[subQ1,subQ0]});Q50=makeQuery(id+"F0.imprint","IMPRINT",FACE,{"disambiguationData":[TD([[makeQuery(id+"F0.imprint","IMPRINT",EDGE,{"disambiguationData":[TD([[subQ2,-1.0]])],"derivedFrom":subQ1}),-1.0]])]});}
            var Q51;
            {var subQ0=sQuery(id+"F0.wireOp",EDGE,"E4.15.0");var subQ1=sQuery(id+"F0.wireOp",EDGE,"E2.0");var subQ2=makeQuery(id+"F0.imprint","INTERSECT",VERTEX,{"disambiguationData":[OD(0.0)],"derivedFrom":[subQ1,subQ0]});Q51=makeQuery(id+"F0.imprint","IMPRINT",FACE,{"disambiguationData":[TD([[makeQuery(id+"F0.imprint","IMPRINT",EDGE,{"disambiguationData":[TD([[subQ2,-1.0]])],"derivedFrom":subQ1}),-1.0]])]});}
            var Q52;
            {var subQ0=sQuery(id+"F0.wireOp",EDGE,"E4.14.0");var subQ1=sQuery(id+"F0.wireOp",EDGE,"E2.0");var subQ2=makeQuery(id+"F0.imprint","INTERSECT",VERTEX,{"disambiguationData":[OD(0.0)],"derivedFrom":[subQ1,subQ0]});Q52=makeQuery(id+"F0.imprint","IMPRINT",FACE,{"disambiguationData":[TD([[makeQuery(id+"F0.imprint","IMPRINT",EDGE,{"disambiguationData":[TD([[subQ2,-1.0]])],"derivedFrom":subQ1}),1.0]])]});}
            var Q53;
            {var subQ0=sQuery(id+"F0.wireOp",EDGE,"E6.6.0");var subQ1=sQuery(id+"F0.wireOp",EDGE,"E2.0");var subQ2=makeQuery(id+"F0.imprint","INTERSECT",VERTEX,{"disambiguationData":[OD(0.0)],"derivedFrom":[subQ1,subQ0]});Q53=makeQuery(id+"F0.imprint","IMPRINT",FACE,{"disambiguationData":[TD([[makeQuery(id+"F0.imprint","IMPRINT",EDGE,{"disambiguationData":[TD([[subQ2,-1.0]])],"derivedFrom":subQ1}),1.0]])]});}
            var Q54;
            {var subQ0=sQuery(id+"F0.wireOp",EDGE,"E6.6.0");var subQ1=sQuery(id+"F0.wireOp",EDGE,"E2.0");var subQ2=makeQuery(id+"F0.imprint","INTERSECT",VERTEX,{"disambiguationData":[OD(0.0)],"derivedFrom":[subQ1,subQ0]});Q54=makeQuery(id+"F0.imprint","IMPRINT",FACE,{"disambiguationData":[TD([[makeQuery(id+"F0.imprint","IMPRINT",EDGE,{"disambiguationData":[TD([[subQ2,-1.0]])],"derivedFrom":subQ1}),-1.0]])]});}
            var Q55;
            {var subQ0=sQuery(id+"F0.wireOp",EDGE,"E4.14.0");var subQ1=sQuery(id+"F0.wireOp",EDGE,"E2.0");var subQ2=makeQuery(id+"F0.imprint","INTERSECT",VERTEX,{"disambiguationData":[OD(0.0)],"derivedFrom":[subQ1,subQ0]});Q55=makeQuery(id+"F0.imprint","IMPRINT",FACE,{"disambiguationData":[TD([[makeQuery(id+"F0.imprint","IMPRINT",EDGE,{"disambiguationData":[TD([[subQ2,-1.0]])],"derivedFrom":subQ1}),-1.0]])]});}
            var Q56;
            {var subQ0=sQuery(id+"F0.wireOp",EDGE,"E4.13.0");var subQ1=sQuery(id+"F0.wireOp",EDGE,"E2.0");var subQ2=makeQuery(id+"F0.imprint","INTERSECT",VERTEX,{"disambiguationData":[OD(0.0)],"derivedFrom":[subQ1,subQ0]});Q56=makeQuery(id+"F0.imprint","IMPRINT",FACE,{"disambiguationData":[TD([[makeQuery(id+"F0.imprint","IMPRINT",EDGE,{"disambiguationData":[TD([[subQ2,-1.0]])],"derivedFrom":subQ1}),-1.0]])]});}
            var Q57;
            {var subQ0=sQuery(id+"F0.wireOp",EDGE,"E6.5.0");var subQ1=sQuery(id+"F0.wireOp",EDGE,"E2.0");var subQ2=makeQuery(id+"F0.imprint","INTERSECT",VERTEX,{"disambiguationData":[OD(0.0)],"derivedFrom":[subQ1,subQ0]});Q57=makeQuery(id+"F0.imprint","IMPRINT",FACE,{"disambiguationData":[TD([[makeQuery(id+"F0.imprint","IMPRINT",EDGE,{"disambiguationData":[TD([[subQ2,-1.0]])],"derivedFrom":subQ1}),-1.0]])]});}
            var Q58;
            {var subQ0=sQuery(id+"F0.wireOp",EDGE,"E6.5.0");var subQ1=sQuery(id+"F0.wireOp",EDGE,"E2.0");var subQ2=makeQuery(id+"F0.imprint","INTERSECT",VERTEX,{"disambiguationData":[OD(0.0)],"derivedFrom":[subQ1,subQ0]});Q58=makeQuery(id+"F0.imprint","IMPRINT",FACE,{"disambiguationData":[TD([[makeQuery(id+"F0.imprint","IMPRINT",EDGE,{"disambiguationData":[TD([[subQ2,-1.0]])],"derivedFrom":subQ1}),1.0]])]});}
            var Q59;
            {var subQ0=sQuery(id+"F0.wireOp",EDGE,"E4.13.0");var subQ1=sQuery(id+"F0.wireOp",EDGE,"E2.0");var subQ2=makeQuery(id+"F0.imprint","INTERSECT",VERTEX,{"disambiguationData":[OD(0.0)],"derivedFrom":[subQ1,subQ0]});Q59=makeQuery(id+"F0.imprint","IMPRINT",FACE,{"disambiguationData":[TD([[makeQuery(id+"F0.imprint","IMPRINT",EDGE,{"disambiguationData":[TD([[subQ2,-1.0]])],"derivedFrom":subQ1}),1.0]])]});}
            var Q60;
            {var subQ0=sQuery(id+"F0.wireOp",EDGE,"E4.12.0");var subQ1=sQuery(id+"F0.wireOp",EDGE,"E2.0");var subQ2=makeQuery(id+"F0.imprint","INTERSECT",VERTEX,{"disambiguationData":[OD(0.0)],"derivedFrom":[subQ1,subQ0]});Q60=makeQuery(id+"F0.imprint","IMPRINT",FACE,{"disambiguationData":[TD([[makeQuery(id+"F0.imprint","IMPRINT",EDGE,{"disambiguationData":[TD([[subQ2,1.0]])],"derivedFrom":subQ1}),1.0]])]});}
            var Q61;
            {var subQ0=sQuery(id+"F0.wireOp",EDGE,"E6.4.0");var subQ1=sQuery(id+"F0.wireOp",EDGE,"E2.0");var subQ2=makeQuery(id+"F0.imprint","INTERSECT",VERTEX,{"disambiguationData":[OD(0.0)],"derivedFrom":[subQ1,subQ0]});Q61=makeQuery(id+"F0.imprint","IMPRINT",FACE,{"disambiguationData":[TD([[makeQuery(id+"F0.imprint","IMPRINT",EDGE,{"disambiguationData":[TD([[subQ2,1.0]])],"derivedFrom":subQ1}),1.0]])]});}
            var Q62;
            {var subQ0=sQuery(id+"F0.wireOp",EDGE,"E6.4.0");var subQ1=sQuery(id+"F0.wireOp",EDGE,"E2.0");var subQ2=makeQuery(id+"F0.imprint","INTERSECT",VERTEX,{"disambiguationData":[OD(0.0)],"derivedFrom":[subQ1,subQ0]});Q62=makeQuery(id+"F0.imprint","IMPRINT",FACE,{"disambiguationData":[TD([[makeQuery(id+"F0.imprint","IMPRINT",EDGE,{"disambiguationData":[TD([[subQ2,1.0]])],"derivedFrom":subQ1}),-1.0]])]});}
            var Q63;
            {var subQ0=sQuery(id+"F0.wireOp",EDGE,"E4.12.0");var subQ1=sQuery(id+"F0.wireOp",EDGE,"E2.0");var subQ2=makeQuery(id+"F0.imprint","INTERSECT",VERTEX,{"disambiguationData":[OD(0.0)],"derivedFrom":[subQ1,subQ0]});Q63=makeQuery(id+"F0.imprint","IMPRINT",FACE,{"disambiguationData":[TD([[makeQuery(id+"F0.imprint","IMPRINT",EDGE,{"disambiguationData":[TD([[subQ2,1.0]])],"derivedFrom":subQ1}),-1.0]])]});}
            extrude(context, id + "F4", {"entities" : qUnion([Q0, Q1, Q2, Q3, Q4, Q5, Q6, Q7, Q8, Q9, Q10, Q11, Q12, Q13, Q14, Q15, Q16, Q17, Q18, Q19, Q20, Q21, Q22, Q23, Q24, Q25, Q26, Q27, Q28, Q29, Q30, Q31, Q32, Q33, Q34, Q35, Q36, Q37, Q38, Q39, Q40, Q41, Q42, Q43, Q44, Q45, Q46, Q47, Q48, Q49, Q50, Q51, Q52, Q53, Q54, Q55, Q56, Q57, Q58, Q59, Q60, Q61, Q62, Q63]), "oppositeDirection" : true, "depth" : 5 * mm, "hasSecondDirection" : true, "secondDirectionOppositeDirection" : true, "secondDirectionDepth" : .12 * mm});
        }
        {
            var Q0;
            Q0=makeQuery(id+"F1.opExtrude","CAP_EDGE",EDGE,{"disambiguationData":[OSD([sQuery(id+"F0.wireOp",EDGE,"E4.2.0")])],"isStart":false});
            var Q1;
            Q1=makeQuery(id+"F1.opExtrude","CAP_EDGE",EDGE,{"disambiguationData":[OSD([sQuery(id+"F0.wireOp",EDGE,"E4.1.0")])],"isStart":false});
            var Q2;
            Q2=makeQuery(id+"F1.opExtrude","CAP_EDGE",EDGE,{"disambiguationData":[OSD([sQuery(id+"F0.wireOp",EDGE,"E3")])],"isStart":false});
            var Q3;
            Q3=makeQuery(id+"F1.opExtrude","CAP_EDGE",EDGE,{"disambiguationData":[OSD([sQuery(id+"F0.wireOp",EDGE,"E4.15.0")])],"isStart":false});
            var Q4;
            Q4=makeQuery(id+"F1.opExtrude","CAP_EDGE",EDGE,{"disambiguationData":[OSD([sQuery(id+"F0.wireOp",EDGE,"E4.14.0")])],"isStart":false});
            var Q5;
            Q5=makeQuery(id+"F1.opExtrude","CAP_EDGE",EDGE,{"disambiguationData":[OSD([sQuery(id+"F0.wireOp",EDGE,"E4.13.0")])],"isStart":false});
            var Q6;
            Q6=makeQuery(id+"F1.opExtrude","CAP_EDGE",EDGE,{"disambiguationData":[OSD([sQuery(id+"F0.wireOp",EDGE,"E4.12.0")])],"isStart":false});
            var Q7;
            Q7=makeQuery(id+"F1.opExtrude","CAP_EDGE",EDGE,{"disambiguationData":[OSD([sQuery(id+"F0.wireOp",EDGE,"E4.11.0")])],"isStart":false});
            var Q8;
            Q8=makeQuery(id+"F1.opExtrude","CAP_EDGE",EDGE,{"disambiguationData":[OSD([sQuery(id+"F0.wireOp",EDGE,"E4.10.0")])],"isStart":false});
            var Q9;
            Q9=makeQuery(id+"F1.opExtrude","CAP_EDGE",EDGE,{"disambiguationData":[OSD([sQuery(id+"F0.wireOp",EDGE,"E4.9.0")])],"isStart":false});
            var Q10;
            Q10=makeQuery(id+"F1.opExtrude","CAP_EDGE",EDGE,{"disambiguationData":[OSD([sQuery(id+"F0.wireOp",EDGE,"E4.8.0")])],"isStart":false});
            var Q11;
            Q11=makeQuery(id+"F1.opExtrude","CAP_EDGE",EDGE,{"disambiguationData":[OSD([sQuery(id+"F0.wireOp",EDGE,"E4.7.0")])],"isStart":false});
            var Q12;
            Q12=makeQuery(id+"F1.opExtrude","CAP_EDGE",EDGE,{"disambiguationData":[OSD([sQuery(id+"F0.wireOp",EDGE,"E4.6.0")])],"isStart":false});
            var Q13;
            Q13=makeQuery(id+"F1.opExtrude","CAP_EDGE",EDGE,{"disambiguationData":[OSD([sQuery(id+"F0.wireOp",EDGE,"E4.5.0")])],"isStart":false});
            var Q14;
            Q14=makeQuery(id+"F1.opExtrude","CAP_EDGE",EDGE,{"disambiguationData":[OSD([sQuery(id+"F0.wireOp",EDGE,"E4.4.0")])],"isStart":false});
            var Q15;
            Q15=makeQuery(id+"F1.opExtrude","CAP_EDGE",EDGE,{"disambiguationData":[OSD([sQuery(id+"F0.wireOp",EDGE,"E4.3.0")])],"isStart":false});
            var Q16;
            Q16=makeQuery(id+"F4.opExtrude","CAP_EDGE",EDGE,{"disambiguationData":[OSD([sQuery(id+"F0.wireOp",EDGE,"E4.15.0")])],"isStart":false});
            var Q17;
            Q17=makeQuery(id+"F4.opExtrude","CAP_EDGE",EDGE,{"disambiguationData":[OSD([sQuery(id+"F0.wireOp",EDGE,"E3")])],"isStart":false});
            var Q18;
            Q18=makeQuery(id+"F4.opExtrude","CAP_EDGE",EDGE,{"disambiguationData":[OSD([sQuery(id+"F0.wireOp",EDGE,"E4.1.0")])],"isStart":false});
            var Q19;
            Q19=makeQuery(id+"F4.opExtrude","CAP_EDGE",EDGE,{"disambiguationData":[OSD([sQuery(id+"F0.wireOp",EDGE,"E4.2.0")])],"isStart":false});
            var Q20;
            Q20=makeQuery(id+"F4.opExtrude","CAP_EDGE",EDGE,{"disambiguationData":[OSD([sQuery(id+"F0.wireOp",EDGE,"E4.3.0")])],"isStart":false});
            var Q21;
            Q21=makeQuery(id+"F4.opExtrude","CAP_EDGE",EDGE,{"disambiguationData":[OSD([sQuery(id+"F0.wireOp",EDGE,"E4.4.0")])],"isStart":false});
            var Q22;
            Q22=makeQuery(id+"F4.opExtrude","CAP_EDGE",EDGE,{"disambiguationData":[OSD([sQuery(id+"F0.wireOp",EDGE,"E4.5.0")])],"isStart":false});
            var Q23;
            Q23=makeQuery(id+"F4.opExtrude","CAP_EDGE",EDGE,{"disambiguationData":[OSD([sQuery(id+"F0.wireOp",EDGE,"E4.6.0")])],"isStart":false});
            var Q24;
            Q24=makeQuery(id+"F4.opExtrude","CAP_EDGE",EDGE,{"disambiguationData":[OSD([sQuery(id+"F0.wireOp",EDGE,"E4.7.0")])],"isStart":false});
            var Q25;
            Q25=makeQuery(id+"F4.opExtrude","CAP_EDGE",EDGE,{"disambiguationData":[OSD([sQuery(id+"F0.wireOp",EDGE,"E4.8.0")])],"isStart":false});
            var Q26;
            Q26=makeQuery(id+"F4.opExtrude","CAP_EDGE",EDGE,{"disambiguationData":[OSD([sQuery(id+"F0.wireOp",EDGE,"E4.9.0")])],"isStart":false});
            var Q27;
            Q27=makeQuery(id+"F4.opExtrude","CAP_EDGE",EDGE,{"disambiguationData":[OSD([sQuery(id+"F0.wireOp",EDGE,"E4.10.0")])],"isStart":false});
            var Q28;
            Q28=makeQuery(id+"F4.opExtrude","CAP_EDGE",EDGE,{"disambiguationData":[OSD([sQuery(id+"F0.wireOp",EDGE,"E4.11.0")])],"isStart":false});
            var Q29;
            Q29=makeQuery(id+"F4.opExtrude","CAP_EDGE",EDGE,{"disambiguationData":[OSD([sQuery(id+"F0.wireOp",EDGE,"E4.12.0")])],"isStart":false});
            var Q30;
            Q30=makeQuery(id+"F4.opExtrude","CAP_EDGE",EDGE,{"disambiguationData":[OSD([sQuery(id+"F0.wireOp",EDGE,"E4.13.0")])],"isStart":false});
            var Q31;
            Q31=makeQuery(id+"F4.opExtrude","CAP_EDGE",EDGE,{"disambiguationData":[OSD([sQuery(id+"F0.wireOp",EDGE,"E4.14.0")])],"isStart":false});
            fillet(context, id + "F5", {"entities" : qUnion([Q0, Q1, Q2, Q3, Q4, Q5, Q6, Q7, Q8, Q9, Q10, Q11, Q12, Q13, Q14, Q15, Q16, Q17, Q18, Q19, Q20, Q21, Q22, Q23, Q24, Q25, Q26, Q27, Q28, Q29, Q30, Q31]), "radius" : 2 * mm, "tangentPropagation" : true, "allowEdgeOverflow" : false});
        }
        {
            var Q0;
            {var subQ0=sQuery(id+"F0.wireOp",EDGE,"E6.3.0");var subQ1=sQuery(id+"F0.wireOp",EDGE,"E2.0");var subQ2=makeQuery(id+"F0.imprint","INTERSECT",VERTEX,{"disambiguationData":[OD(0.0)],"derivedFrom":[subQ1,subQ0]});Q0=makeQuery(id+"F0.imprint","IMPRINT",FACE,{"disambiguationData":[TD([[makeQuery(id+"F0.imprint","IMPRINT",EDGE,{"disambiguationData":[TD([[subQ2,-1.0]])],"derivedFrom":subQ1}),-1.0]])]});}
            var Q1;
            {var subQ0=sQuery(id+"F0.wireOp",EDGE,"E6.3.0");var subQ1=sQuery(id+"F0.wireOp",EDGE,"E2.0");var subQ2=makeQuery(id+"F0.imprint","INTERSECT",VERTEX,{"disambiguationData":[OD(0.0)],"derivedFrom":[subQ1,subQ0]});Q1=makeQuery(id+"F0.imprint","IMPRINT",FACE,{"disambiguationData":[TD([[makeQuery(id+"F0.imprint","IMPRINT",EDGE,{"disambiguationData":[TD([[subQ2,-1.0]])],"derivedFrom":subQ1}),1.0]])]});}
            var Q2;
            {var subQ0=sQuery(id+"F0.wireOp",EDGE,"E6.4.0");var subQ1=sQuery(id+"F0.wireOp",EDGE,"E2.0");var subQ2=makeQuery(id+"F0.imprint","INTERSECT",VERTEX,{"disambiguationData":[OD(0.0)],"derivedFrom":[subQ1,subQ0]});Q2=makeQuery(id+"F0.imprint","IMPRINT",FACE,{"disambiguationData":[TD([[makeQuery(id+"F0.imprint","IMPRINT",EDGE,{"disambiguationData":[TD([[subQ2,1.0]])],"derivedFrom":subQ1}),1.0]])]});}
            var Q3;
            {var subQ0=sQuery(id+"F0.wireOp",EDGE,"E6.4.0");var subQ1=sQuery(id+"F0.wireOp",EDGE,"E2.0");var subQ2=makeQuery(id+"F0.imprint","INTERSECT",VERTEX,{"disambiguationData":[OD(0.0)],"derivedFrom":[subQ1,subQ0]});Q3=makeQuery(id+"F0.imprint","IMPRINT",FACE,{"disambiguationData":[TD([[makeQuery(id+"F0.imprint","IMPRINT",EDGE,{"disambiguationData":[TD([[subQ2,1.0]])],"derivedFrom":subQ1}),-1.0]])]});}
            var Q4;
            {var subQ0=sQuery(id+"F0.wireOp",EDGE,"E6.5.0");var subQ1=sQuery(id+"F0.wireOp",EDGE,"E2.0");var subQ2=makeQuery(id+"F0.imprint","INTERSECT",VERTEX,{"disambiguationData":[OD(0.0)],"derivedFrom":[subQ1,subQ0]});Q4=makeQuery(id+"F0.imprint","IMPRINT",FACE,{"disambiguationData":[TD([[makeQuery(id+"F0.imprint","IMPRINT",EDGE,{"disambiguationData":[TD([[subQ2,-1.0]])],"derivedFrom":subQ1}),-1.0]])]});}
            var Q5;
            {var subQ0=sQuery(id+"F0.wireOp",EDGE,"E6.5.0");var subQ1=sQuery(id+"F0.wireOp",EDGE,"E2.0");var subQ2=makeQuery(id+"F0.imprint","INTERSECT",VERTEX,{"disambiguationData":[OD(0.0)],"derivedFrom":[subQ1,subQ0]});Q5=makeQuery(id+"F0.imprint","IMPRINT",FACE,{"disambiguationData":[TD([[makeQuery(id+"F0.imprint","IMPRINT",EDGE,{"disambiguationData":[TD([[subQ2,-1.0]])],"derivedFrom":subQ1}),1.0]])]});}
            var Q6;
            {var subQ0=sQuery(id+"F0.wireOp",EDGE,"E6.6.0");var subQ1=sQuery(id+"F0.wireOp",EDGE,"E2.0");var subQ2=makeQuery(id+"F0.imprint","INTERSECT",VERTEX,{"disambiguationData":[OD(0.0)],"derivedFrom":[subQ1,subQ0]});Q6=makeQuery(id+"F0.imprint","IMPRINT",FACE,{"disambiguationData":[TD([[makeQuery(id+"F0.imprint","IMPRINT",EDGE,{"disambiguationData":[TD([[subQ2,-1.0]])],"derivedFrom":subQ1}),-1.0]])]});}
            var Q7;
            {var subQ0=sQuery(id+"F0.wireOp",EDGE,"E6.6.0");var subQ1=sQuery(id+"F0.wireOp",EDGE,"E2.0");var subQ2=makeQuery(id+"F0.imprint","INTERSECT",VERTEX,{"disambiguationData":[OD(0.0)],"derivedFrom":[subQ1,subQ0]});Q7=makeQuery(id+"F0.imprint","IMPRINT",FACE,{"disambiguationData":[TD([[makeQuery(id+"F0.imprint","IMPRINT",EDGE,{"disambiguationData":[TD([[subQ2,-1.0]])],"derivedFrom":subQ1}),1.0]])]});}
            var Q8;
            {var subQ0=sQuery(id+"F0.wireOp",EDGE,"E6.7.0");var subQ1=sQuery(id+"F0.wireOp",EDGE,"E2.0");var subQ2=makeQuery(id+"F0.imprint","INTERSECT",VERTEX,{"disambiguationData":[OD(0.0)],"derivedFrom":[subQ1,subQ0]});Q8=makeQuery(id+"F0.imprint","IMPRINT",FACE,{"disambiguationData":[TD([[makeQuery(id+"F0.imprint","IMPRINT",EDGE,{"disambiguationData":[TD([[subQ2,-1.0]])],"derivedFrom":subQ1}),-1.0]])]});}
            var Q9;
            {var subQ0=sQuery(id+"F0.wireOp",EDGE,"E6.7.0");var subQ1=sQuery(id+"F0.wireOp",EDGE,"E2.0");var subQ2=makeQuery(id+"F0.imprint","INTERSECT",VERTEX,{"disambiguationData":[OD(0.0)],"derivedFrom":[subQ1,subQ0]});Q9=makeQuery(id+"F0.imprint","IMPRINT",FACE,{"disambiguationData":[TD([[makeQuery(id+"F0.imprint","IMPRINT",EDGE,{"disambiguationData":[TD([[subQ2,-1.0]])],"derivedFrom":subQ1}),1.0]])]});}
            var Q10;
            {var subQ0=sQuery(id+"F0.wireOp",EDGE,"E6.8.0");var subQ1=sQuery(id+"F0.wireOp",EDGE,"E2.0");var subQ2=makeQuery(id+"F0.imprint","INTERSECT",VERTEX,{"disambiguationData":[OD(0.0)],"derivedFrom":[subQ1,subQ0]});Q10=makeQuery(id+"F0.imprint","IMPRINT",FACE,{"disambiguationData":[TD([[makeQuery(id+"F0.imprint","IMPRINT",EDGE,{"disambiguationData":[TD([[subQ2,-1.0]])],"derivedFrom":subQ1}),-1.0]])]});}
            var Q11;
            {var subQ0=sQuery(id+"F0.wireOp",EDGE,"E6.8.0");var subQ1=sQuery(id+"F0.wireOp",EDGE,"E2.0");var subQ2=makeQuery(id+"F0.imprint","INTERSECT",VERTEX,{"disambiguationData":[OD(0.0)],"derivedFrom":[subQ1,subQ0]});Q11=makeQuery(id+"F0.imprint","IMPRINT",FACE,{"disambiguationData":[TD([[makeQuery(id+"F0.imprint","IMPRINT",EDGE,{"disambiguationData":[TD([[subQ2,-1.0]])],"derivedFrom":subQ1}),1.0]])]});}
            var Q12;
            {var subQ0=sQuery(id+"F0.wireOp",EDGE,"E6.9.0");var subQ1=sQuery(id+"F0.wireOp",EDGE,"E2.0");var subQ2=makeQuery(id+"F0.imprint","INTERSECT",VERTEX,{"disambiguationData":[OD(0.0)],"derivedFrom":[subQ1,subQ0]});Q12=makeQuery(id+"F0.imprint","IMPRINT",FACE,{"disambiguationData":[TD([[makeQuery(id+"F0.imprint","IMPRINT",EDGE,{"disambiguationData":[TD([[subQ2,-1.0]])],"derivedFrom":subQ1}),-1.0]])]});}
            var Q13;
            {var subQ0=sQuery(id+"F0.wireOp",EDGE,"E6.9.0");var subQ1=sQuery(id+"F0.wireOp",EDGE,"E2.0");var subQ2=makeQuery(id+"F0.imprint","INTERSECT",VERTEX,{"disambiguationData":[OD(0.0)],"derivedFrom":[subQ1,subQ0]});Q13=makeQuery(id+"F0.imprint","IMPRINT",FACE,{"disambiguationData":[TD([[makeQuery(id+"F0.imprint","IMPRINT",EDGE,{"disambiguationData":[TD([[subQ2,-1.0]])],"derivedFrom":subQ1}),1.0]])]});}
            var Q14;
            {var subQ0=sQuery(id+"F0.wireOp",EDGE,"E6.10.0");var subQ1=sQuery(id+"F0.wireOp",EDGE,"E2.0");var subQ2=makeQuery(id+"F0.imprint","INTERSECT",VERTEX,{"disambiguationData":[OD(0.0)],"derivedFrom":[subQ1,subQ0]});Q14=makeQuery(id+"F0.imprint","IMPRINT",FACE,{"disambiguationData":[TD([[makeQuery(id+"F0.imprint","IMPRINT",EDGE,{"disambiguationData":[TD([[subQ2,-1.0]])],"derivedFrom":subQ1}),1.0]])]});}
            var Q15;
            {var subQ0=sQuery(id+"F0.wireOp",EDGE,"E6.10.0");var subQ1=sQuery(id+"F0.wireOp",EDGE,"E2.0");var subQ2=makeQuery(id+"F0.imprint","INTERSECT",VERTEX,{"disambiguationData":[OD(0.0)],"derivedFrom":[subQ1,subQ0]});Q15=makeQuery(id+"F0.imprint","IMPRINT",FACE,{"disambiguationData":[TD([[makeQuery(id+"F0.imprint","IMPRINT",EDGE,{"disambiguationData":[TD([[subQ2,-1.0]])],"derivedFrom":subQ1}),-1.0]])]});}
            var Q16;
            {var subQ0=sQuery(id+"F0.wireOp",EDGE,"E6.11.0");var subQ1=sQuery(id+"F0.wireOp",EDGE,"E2.0");var subQ2=makeQuery(id+"F0.imprint","INTERSECT",VERTEX,{"disambiguationData":[OD(0.0)],"derivedFrom":[subQ1,subQ0]});Q16=makeQuery(id+"F0.imprint","IMPRINT",FACE,{"disambiguationData":[TD([[makeQuery(id+"F0.imprint","IMPRINT",EDGE,{"disambiguationData":[TD([[subQ2,-1.0]])],"derivedFrom":subQ1}),1.0]])]});}
            var Q17;
            {var subQ0=sQuery(id+"F0.wireOp",EDGE,"E6.11.0");var subQ1=sQuery(id+"F0.wireOp",EDGE,"E2.0");var subQ2=makeQuery(id+"F0.imprint","INTERSECT",VERTEX,{"disambiguationData":[OD(0.0)],"derivedFrom":[subQ1,subQ0]});Q17=makeQuery(id+"F0.imprint","IMPRINT",FACE,{"disambiguationData":[TD([[makeQuery(id+"F0.imprint","IMPRINT",EDGE,{"disambiguationData":[TD([[subQ2,-1.0]])],"derivedFrom":subQ1}),-1.0]])]});}
            var Q18;
            {var subQ0=sQuery(id+"F0.wireOp",EDGE,"E6.12.0");var subQ1=sQuery(id+"F0.wireOp",EDGE,"E2.0");var subQ2=makeQuery(id+"F0.imprint","INTERSECT",VERTEX,{"disambiguationData":[OD(0.0)],"derivedFrom":[subQ1,subQ0]});Q18=makeQuery(id+"F0.imprint","IMPRINT",FACE,{"disambiguationData":[TD([[makeQuery(id+"F0.imprint","IMPRINT",EDGE,{"disambiguationData":[TD([[subQ2,-1.0]])],"derivedFrom":subQ1}),-1.0]])]});}
            var Q19;
            {var subQ0=sQuery(id+"F0.wireOp",EDGE,"E6.12.0");var subQ1=sQuery(id+"F0.wireOp",EDGE,"E2.0");var subQ2=makeQuery(id+"F0.imprint","INTERSECT",VERTEX,{"disambiguationData":[OD(0.0)],"derivedFrom":[subQ1,subQ0]});Q19=makeQuery(id+"F0.imprint","IMPRINT",FACE,{"disambiguationData":[TD([[makeQuery(id+"F0.imprint","IMPRINT",EDGE,{"disambiguationData":[TD([[subQ2,-1.0]])],"derivedFrom":subQ1}),1.0]])]});}
            var Q20;
            {var subQ0=sQuery(id+"F0.wireOp",EDGE,"E6.13.0");var subQ1=sQuery(id+"F0.wireOp",EDGE,"E2.0");var subQ2=makeQuery(id+"F0.imprint","INTERSECT",VERTEX,{"disambiguationData":[OD(0.0)],"derivedFrom":[subQ1,subQ0]});Q20=makeQuery(id+"F0.imprint","IMPRINT",FACE,{"disambiguationData":[TD([[makeQuery(id+"F0.imprint","IMPRINT",EDGE,{"disambiguationData":[TD([[subQ2,-1.0]])],"derivedFrom":subQ1}),1.0]])]});}
            var Q21;
            {var subQ0=sQuery(id+"F0.wireOp",EDGE,"E6.13.0");var subQ1=sQuery(id+"F0.wireOp",EDGE,"E2.0");var subQ2=makeQuery(id+"F0.imprint","INTERSECT",VERTEX,{"disambiguationData":[OD(0.0)],"derivedFrom":[subQ1,subQ0]});Q21=makeQuery(id+"F0.imprint","IMPRINT",FACE,{"disambiguationData":[TD([[makeQuery(id+"F0.imprint","IMPRINT",EDGE,{"disambiguationData":[TD([[subQ2,-1.0]])],"derivedFrom":subQ1}),-1.0]])]});}
            var Q22;
            {var subQ0=sQuery(id+"F0.wireOp",EDGE,"E6.14.0");var subQ1=sQuery(id+"F0.wireOp",EDGE,"E2.0");var subQ2=makeQuery(id+"F0.imprint","INTERSECT",VERTEX,{"disambiguationData":[OD(0.0)],"derivedFrom":[subQ1,subQ0]});Q22=makeQuery(id+"F0.imprint","IMPRINT",FACE,{"disambiguationData":[TD([[makeQuery(id+"F0.imprint","IMPRINT",EDGE,{"disambiguationData":[TD([[subQ2,-1.0]])],"derivedFrom":subQ1}),1.0]])]});}
            var Q23;
            {var subQ0=sQuery(id+"F0.wireOp",EDGE,"E6.14.0");var subQ1=sQuery(id+"F0.wireOp",EDGE,"E2.0");var subQ2=makeQuery(id+"F0.imprint","INTERSECT",VERTEX,{"disambiguationData":[OD(0.0)],"derivedFrom":[subQ1,subQ0]});Q23=makeQuery(id+"F0.imprint","IMPRINT",FACE,{"disambiguationData":[TD([[makeQuery(id+"F0.imprint","IMPRINT",EDGE,{"disambiguationData":[TD([[subQ2,-1.0]])],"derivedFrom":subQ1}),-1.0]])]});}
            var Q24;
            {var subQ0=sQuery(id+"F0.wireOp",EDGE,"E6.15.0");var subQ1=sQuery(id+"F0.wireOp",EDGE,"E2.0");var subQ2=makeQuery(id+"F0.imprint","INTERSECT",VERTEX,{"disambiguationData":[OD(0.0)],"derivedFrom":[subQ1,subQ0]});Q24=makeQuery(id+"F0.imprint","IMPRINT",FACE,{"disambiguationData":[TD([[makeQuery(id+"F0.imprint","IMPRINT",EDGE,{"disambiguationData":[TD([[subQ2,-1.0]])],"derivedFrom":subQ1}),1.0]])]});}
            var Q25;
            {var subQ0=sQuery(id+"F0.wireOp",EDGE,"E6.15.0");var subQ1=sQuery(id+"F0.wireOp",EDGE,"E2.0");var subQ2=makeQuery(id+"F0.imprint","INTERSECT",VERTEX,{"disambiguationData":[OD(0.0)],"derivedFrom":[subQ1,subQ0]});Q25=makeQuery(id+"F0.imprint","IMPRINT",FACE,{"disambiguationData":[TD([[makeQuery(id+"F0.imprint","IMPRINT",EDGE,{"disambiguationData":[TD([[subQ2,-1.0]])],"derivedFrom":subQ1}),-1.0]])]});}
            var Q26;
            {var subQ0=sQuery(id+"F0.wireOp",EDGE,"E5.0");var subQ1=sQuery(id+"F0.wireOp",EDGE,"E2.0");var subQ2=makeQuery(id+"F0.imprint","INTERSECT",VERTEX,{"disambiguationData":[OD(0.0)],"derivedFrom":[subQ1,subQ0]});Q26=makeQuery(id+"F0.imprint","IMPRINT",FACE,{"disambiguationData":[TD([[makeQuery(id+"F0.imprint","IMPRINT",EDGE,{"disambiguationData":[TD([[subQ2,-1.0]])],"derivedFrom":subQ1}),1.0]])]});}
            var Q27;
            {var subQ0=sQuery(id+"F0.wireOp",EDGE,"E5.0");var subQ1=sQuery(id+"F0.wireOp",EDGE,"E2.0");var subQ2=makeQuery(id+"F0.imprint","INTERSECT",VERTEX,{"disambiguationData":[OD(0.0)],"derivedFrom":[subQ1,subQ0]});Q27=makeQuery(id+"F0.imprint","IMPRINT",FACE,{"disambiguationData":[TD([[makeQuery(id+"F0.imprint","IMPRINT",EDGE,{"disambiguationData":[TD([[subQ2,-1.0]])],"derivedFrom":subQ1}),-1.0]])]});}
            var Q28;
            {var subQ0=sQuery(id+"F0.wireOp",EDGE,"E6.1.0");var subQ1=sQuery(id+"F0.wireOp",EDGE,"E2.0");var subQ2=makeQuery(id+"F0.imprint","INTERSECT",VERTEX,{"disambiguationData":[OD(0.0)],"derivedFrom":[subQ1,subQ0]});Q28=makeQuery(id+"F0.imprint","IMPRINT",FACE,{"disambiguationData":[TD([[makeQuery(id+"F0.imprint","IMPRINT",EDGE,{"disambiguationData":[TD([[subQ2,-1.0]])],"derivedFrom":subQ1}),1.0]])]});}
            var Q29;
            {var subQ0=sQuery(id+"F0.wireOp",EDGE,"E6.1.0");var subQ1=sQuery(id+"F0.wireOp",EDGE,"E2.0");var subQ2=makeQuery(id+"F0.imprint","INTERSECT",VERTEX,{"disambiguationData":[OD(0.0)],"derivedFrom":[subQ1,subQ0]});Q29=makeQuery(id+"F0.imprint","IMPRINT",FACE,{"disambiguationData":[TD([[makeQuery(id+"F0.imprint","IMPRINT",EDGE,{"disambiguationData":[TD([[subQ2,-1.0]])],"derivedFrom":subQ1}),-1.0]])]});}
            var Q30;
            {var subQ0=sQuery(id+"F0.wireOp",EDGE,"E6.2.0");var subQ1=sQuery(id+"F0.wireOp",EDGE,"E2.0");var subQ2=makeQuery(id+"F0.imprint","INTERSECT",VERTEX,{"disambiguationData":[OD(0.0)],"derivedFrom":[subQ1,subQ0]});Q30=makeQuery(id+"F0.imprint","IMPRINT",FACE,{"disambiguationData":[TD([[makeQuery(id+"F0.imprint","IMPRINT",EDGE,{"disambiguationData":[TD([[subQ2,-1.0]])],"derivedFrom":subQ1}),1.0]])]});}
            var Q31;
            {var subQ0=sQuery(id+"F0.wireOp",EDGE,"E6.2.0");var subQ1=sQuery(id+"F0.wireOp",EDGE,"E2.0");var subQ2=makeQuery(id+"F0.imprint","INTERSECT",VERTEX,{"disambiguationData":[OD(0.0)],"derivedFrom":[subQ1,subQ0]});Q31=makeQuery(id+"F0.imprint","IMPRINT",FACE,{"disambiguationData":[TD([[makeQuery(id+"F0.imprint","IMPRINT",EDGE,{"disambiguationData":[TD([[subQ2,-1.0]])],"derivedFrom":subQ1}),-1.0]])]});}
            extrude(context, id + "F6", {"entities" : qUnion([Q0, Q1, Q2, Q3, Q4, Q5, Q6, Q7, Q8, Q9, Q10, Q11, Q12, Q13, Q14, Q15, Q16, Q17, Q18, Q19, Q20, Q21, Q22, Q23, Q24, Q25, Q26, Q27, Q28, Q29, Q30, Q31]), "depth" : .4 * mm, "hasSecondDirection" : true, "secondDirectionOppositeDirection" : true, "secondDirectionDepth" : .4 * mm});
        }
    });
